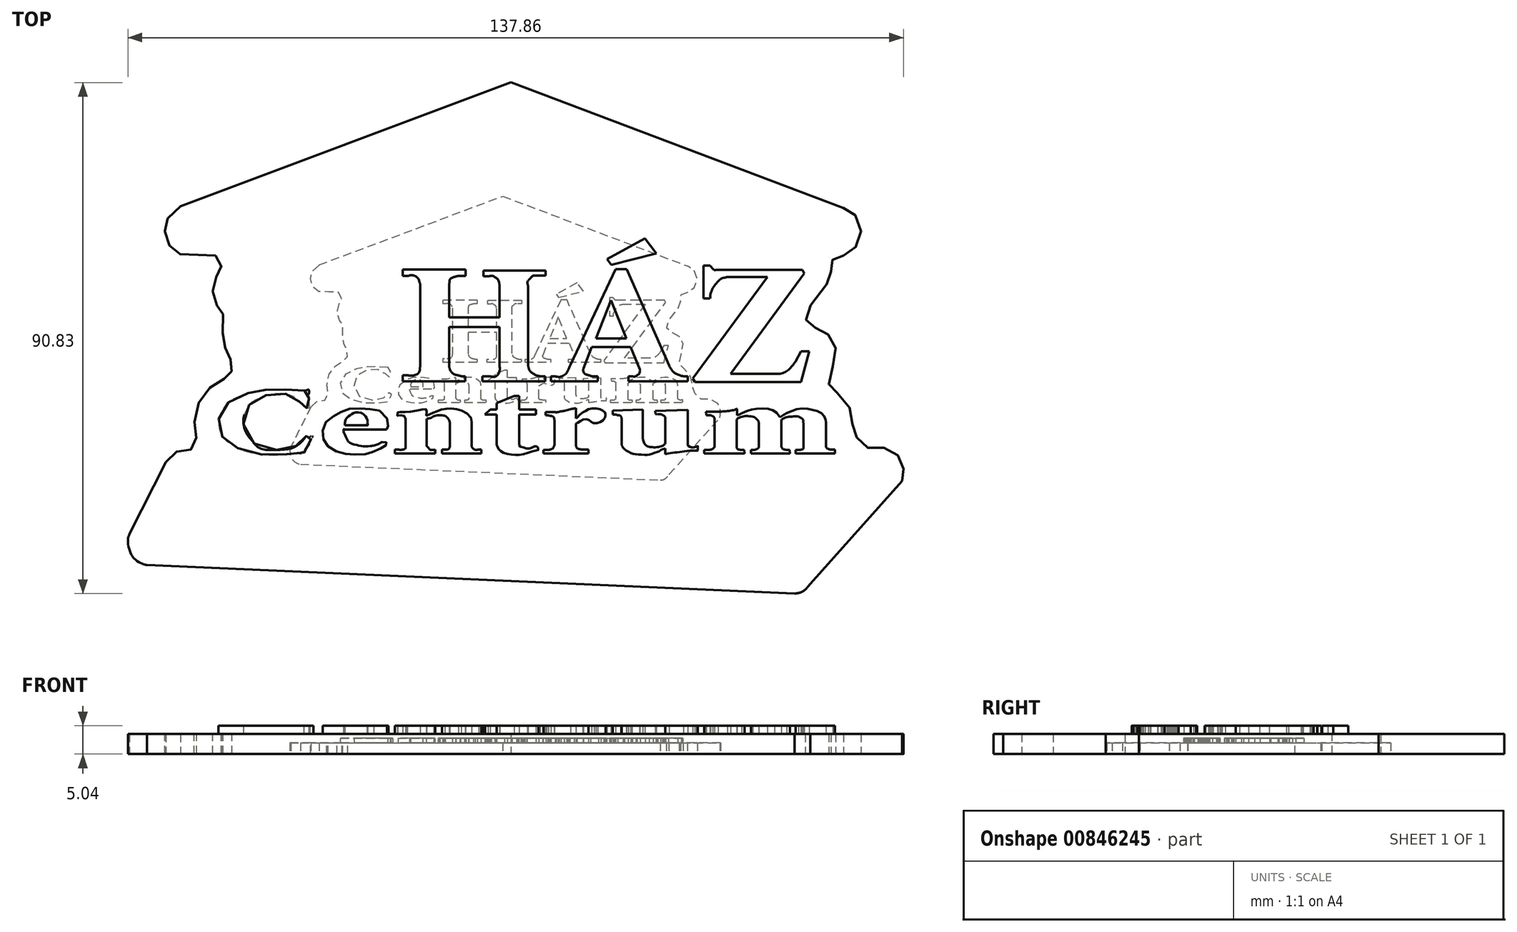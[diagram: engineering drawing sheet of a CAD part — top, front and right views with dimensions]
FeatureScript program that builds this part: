
annotation { "Feature Type Name" : "Feature", "Feature Type Description" : "" }
export const myFeature = defineFeature(function(context is Context, id is Id, definition is map)
    precondition{}
    {
        {
            var Q0;
            Q0=qCreatedBy(makeId("Top.planeOp"),FACE);
            var sketch = newSketch(context, id + "F0", { "sketchPlane" : qUnion([Q0])});
            skLineSegment(sketch, "E0", {"start": v(-30.08, 10.5) * mm, "end": v(1.83, 22.46) * mm});
            skLineSegment(sketch, "E1", {"start": v(1.83, 22.46) * mm, "end": v(33.46, 10.5) * mm});
            skLineSegment(sketch, "E2", {"start": v(33.46, 10.5) * mm, "end": v(-30.08, 10.5) * mm});
            skLineSegment(sketch, "E3", {"start": v(-30.08, -13.2) * mm, "end": v(37.96, -13.19) * mm});
            skLineSegment(sketch, "E4", {"start": v(37.96, -13.19) * mm, "end": v(29.5, -22.68) * mm});
            skLineSegment(sketch, "E5", {"start": v(29.5, -22.68) * mm, "end": v(-33.48, -19.9) * mm});
            skLineSegment(sketch, "E6", {"start": v(-33.48, -19.9) * mm, "end": v(-30.08, -13.2) * mm});
            skFitSpline(sketch, "E7", {"points": [v(-25.1, 4.44) * mm, v(-24.51, 4.46) * mm, v(-24.23, 4.28) * mm, v(-24.13, 3.89) * mm, v(-24.05, 0) * mm, v(-24.04, -0.4) * mm, v(-23.47, -1.49) * mm, v(-21.36, -2.34) * mm, v(-19.33, -2.17) * mm, v(-17.82, -0.87) * mm, v(-17.52, 0.4) * mm, v(-17.44, 3.46) * mm, v(-17.44, 3.92) * mm, v(-17.28, 4.2) * mm, v(-16.7, 4.4) * mm, v(-16.38, 4.41) * mm, v(-16.38, 4.8) * mm, v(-16.52, 4.86) * mm, v(-19.36, 4.89) * mm, v(-19.5, 4.87) * mm, v(-19.5, 4.8) * mm, v(-19.5, 4.47) * mm, v(-19.49, 4.38) * mm, v(-19.23, 4.43) * mm, v(-18.68, 4.41) * mm, v(-18.33, 4.24) * mm, v(-18.19, 3.78) * mm, v(-18.19, 3.5) * mm, v(-18.2, 0.13) * mm, v(-18.2, -0.14) * mm, v(-18.42, -0.62) * mm, v(-19.42, -1.46) * mm, v(-20.82, -1.61) * mm, v(-21.7, -1.14) * mm, v(-22.28, -0.2) * mm, v(-22.3, 0.46) * mm, v(-22.3, 0.68) * mm, v(-22.28, 3.9) * mm, v(-22.25, 4.08) * mm, v(-22.12, 4.32) * mm, v(-21.64, 4.43) * mm, v(-21.37, 4.43) * mm, v(-21.31, 4.6) * mm, v(-21.34, 4.74) * mm, v(-21.34, 4.89) * mm, v(-21.52, 4.89) * mm, v(-24.93, 4.84) * mm, v(-25.08, 4.86) * mm, v(-25.13, 4.71) * mm, v(-25.1, 4.44) * mm]});
            skLineSegment(sketch, "E8", {"start": v(-21.44, 5.5) * mm, "end": v(-21.2, 5.16) * mm});
            skLineSegment(sketch, "E9", {"start": v(-21.2, 5.16) * mm, "end": v(-18.55, 5.87) * mm});
            skLineSegment(sketch, "E10", {"start": v(-18.55, 5.87) * mm, "end": v(-19.2, 6.79) * mm});
            skLineSegment(sketch, "E11", {"start": v(-19.2, 6.79) * mm, "end": v(-21.44, 5.5) * mm});
            skLineSegment(sketch, "E12", {"start": v(-15.1, 4.36) * mm, "end": v(-15.63, 4.36) * mm});
            skLineSegment(sketch, "E13", {"start": v(-15.63, 4.36) * mm, "end": v(-15.63, 4.86) * mm});
            skLineSegment(sketch, "E14", {"start": v(-15.63, 4.86) * mm, "end": v(-11.81, 4.86) * mm});
            skLineSegment(sketch, "E15", {"start": v(-11.81, 4.86) * mm, "end": v(-11.81, 4.4) * mm});
            skLineSegment(sketch, "E16", {"start": v(-11.81, 4.4) * mm, "end": v(-12.34, 4.4) * mm});
            skLineSegment(sketch, "E17", {"start": v(-14.68, 4.01) * mm, "end": v(-14.68, -2.04) * mm});
            skLineSegment(sketch, "E18", {"start": v(-12.84, 4) * mm, "end": v(-12.84, -1.76) * mm});
            skFitSpline(sketch, "E19", {"points": [v(-15.1, 4.36) * mm, v(-14.78, 4.36) * mm, v(-14.68, 4.01) * mm], "startDerivative": vector(0.76, 0.17) * mm, "endDerivative": vector(0.08, -0.96) * mm});
            skFitSpline(sketch, "E20", {"points": [v(-12.84, 4) * mm, v(-12.68, 4.32) * mm, v(-12.34, 4.4) * mm], "startDerivative": vector(0.22, 0.75) * mm, "endDerivative": vector(0.8, 0.04) * mm});
            skFitSpline(sketch, "E21", {"points": [v(-14.68, -2.04) * mm, v(-14.68, -2.66) * mm, v(-14.68, -2.79) * mm, v(-15.17, -3.3) * mm, v(-15.78, -3.58) * mm, v(-15.9, -3.58) * mm, v(-15.89, -3.66) * mm, v(-15.9, -3.93) * mm, v(-15.78, -3.95) * mm, v(-15.43, -3.95) * mm, v(-14.92, -3.79) * mm, v(-13.75, -3.09) * mm, v(-13.2, -2.47) * mm, v(-12.84, -1.76) * mm], "startDerivative": vector(-0.26, -8.21) * mm, "endDerivative": vector(3.35, 7.13) * mm});
            skLineSegment(sketch, "E22", {"start": v(-8.39, 6.17) * mm, "end": v(-8.85, 6.17) * mm});
            skLineSegment(sketch, "E23", {"start": v(-8.85, 6.17) * mm, "end": v(-8.85, 6.78) * mm});
            skLineSegment(sketch, "E24", {"start": v(-8.85, 6.78) * mm, "end": v(-2.66, 6.78) * mm});
            skLineSegment(sketch, "E25", {"start": v(-2.66, 6.78) * mm, "end": v(-2.66, 6.17) * mm});
            skLineSegment(sketch, "E26", {"start": v(-2.66, 6.17) * mm, "end": v(-3.36, 6.17) * mm});
            skLineSegment(sketch, "E27", {"start": v(-7.13, 5.37) * mm, "end": v(-7.13, -2.82) * mm});
            skLineSegment(sketch, "E28", {"start": v(-4.27, 5.39) * mm, "end": v(-4.27, 2.06) * mm});
            skLineSegment(sketch, "E29", {"start": v(-4.27, 2.06) * mm, "end": v(0.72, 2.06) * mm});
            skLineSegment(sketch, "E30", {"start": v(0.72, 2.06) * mm, "end": v(0.72, 5.28) * mm});
            skLineSegment(sketch, "E31", {"start": v(-0.41, 6.13) * mm, "end": v(-0.88, 6.13) * mm});
            skLineSegment(sketch, "E32", {"start": v(-0.88, 6.13) * mm, "end": v(-0.88, 6.7) * mm});
            skLineSegment(sketch, "E33", {"start": v(-0.88, 6.7) * mm, "end": v(5.27, 6.7) * mm});
            skLineSegment(sketch, "E34", {"start": v(5.27, 6.7) * mm, "end": v(5.27, 6.19) * mm});
            skLineSegment(sketch, "E35", {"start": v(5.27, 6.19) * mm, "end": v(4.53, 6.19) * mm});
            skLineSegment(sketch, "E36", {"start": v(3.5, 5.2) * mm, "end": v(3.5, -2.7) * mm});
            skLineSegment(sketch, "E37", {"start": v(-4.28, -2.78) * mm, "end": v(-4.28, 1.1) * mm});
            skLineSegment(sketch, "E38", {"start": v(-4.28, 1.1) * mm, "end": v(0.7, 1.1) * mm});
            skLineSegment(sketch, "E39", {"start": v(0.7, 1.1) * mm, "end": v(0.7, -2.6) * mm});
            skLineSegment(sketch, "E40", {"start": v(-8.5, -3.66) * mm, "end": v(-8.85, -3.66) * mm});
            skLineSegment(sketch, "E41", {"start": v(-8.85, -3.66) * mm, "end": v(-8.85, -4.23) * mm});
            skLineSegment(sketch, "E42", {"start": v(-8.85, -4.23) * mm, "end": v(-2.68, -4.23) * mm});
            skLineSegment(sketch, "E43", {"start": v(-2.68, -4.23) * mm, "end": v(-2.68, -3.75) * mm});
            skLineSegment(sketch, "E44", {"start": v(-2.68, -3.75) * mm, "end": v(-3.08, -3.75) * mm});
            skLineSegment(sketch, "E45", {"start": v(-0.67, -3.75) * mm, "end": v(-1, -3.75) * mm});
            skLineSegment(sketch, "E46", {"start": v(-1, -3.75) * mm, "end": v(-1, -4.23) * mm});
            skLineSegment(sketch, "E47", {"start": v(-1, -4.23) * mm, "end": v(5.21, -4.23) * mm});
            skLineSegment(sketch, "E48", {"start": v(5.21, -4.23) * mm, "end": v(5.21, -3.75) * mm});
            skLineSegment(sketch, "E49", {"start": v(5.21, -3.75) * mm, "end": v(4.72, -3.75) * mm});
            skLineSegment(sketch, "E50", {"start": v(6.1, -3.75) * mm, "end": v(5.78, -3.75) * mm});
            skLineSegment(sketch, "E51", {"start": v(5.78, -3.75) * mm, "end": v(5.78, -4.23) * mm});
            skLineSegment(sketch, "E52", {"start": v(5.78, -4.23) * mm, "end": v(10.42, -4.23) * mm});
            skLineSegment(sketch, "E53", {"start": v(10.42, -4.23) * mm, "end": v(10.42, -3.75) * mm});
            skLineSegment(sketch, "E54", {"start": v(10.42, -3.75) * mm, "end": v(10.07, -3.75) * mm});
            skLineSegment(sketch, "E55", {"start": v(7.73, -2.6) * mm, "end": v(12.18, 6.83) * mm});
            skLineSegment(sketch, "E56", {"start": v(12.18, 6.83) * mm, "end": v(13.26, 6.83) * mm});
            skLineSegment(sketch, "E57", {"start": v(13.26, 6.83) * mm, "end": v(17.45, -2.7) * mm});
            skLineSegment(sketch, "E58", {"start": v(10.22, 0) * mm, "end": v(11.72, 3.76) * mm});
            skLineSegment(sketch, "E59", {"start": v(11.72, 3.76) * mm, "end": v(13.22, 0) * mm});
            skLineSegment(sketch, "E60", {"start": v(13.22, 0) * mm, "end": v(10.22, 0) * mm});
            skLineSegment(sketch, "E61", {"start": v(8.99, -3) * mm, "end": v(9.81, -0.88) * mm});
            skLineSegment(sketch, "E62", {"start": v(9.81, -0.88) * mm, "end": v(13.66, -0.88) * mm});
            skLineSegment(sketch, "E63", {"start": v(13.66, -0.88) * mm, "end": v(14.56, -3.07) * mm});
            skLineSegment(sketch, "E64", {"start": v(13.8, -3.75) * mm, "end": v(13.43, -3.75) * mm});
            skLineSegment(sketch, "E65", {"start": v(13.43, -3.75) * mm, "end": v(13.43, -4.23) * mm});
            skLineSegment(sketch, "E66", {"start": v(13.43, -4.23) * mm, "end": v(19.3, -4.23) * mm});
            skLineSegment(sketch, "E67", {"start": v(19.3, -4.23) * mm, "end": v(19.3, -3.75) * mm});
            skLineSegment(sketch, "E68", {"start": v(19.3, -3.75) * mm, "end": v(18.88, -3.75) * mm});
            skLineSegment(sketch, "E69", {"start": v(11.34, 7.83) * mm, "end": v(11.73, 7.26) * mm});
            skLineSegment(sketch, "E70", {"start": v(11.73, 7.26) * mm, "end": v(16.2, 8.38) * mm});
            skLineSegment(sketch, "E71", {"start": v(16.2, 8.38) * mm, "end": v(15.06, 9.86) * mm});
            skLineSegment(sketch, "E72", {"start": v(15.06, 9.86) * mm, "end": v(11.34, 7.83) * mm});
            skLineSegment(sketch, "E73", {"start": v(23.23, 6.07) * mm, "end": v(27.17, 6.07) * mm});
            skLineSegment(sketch, "E74", {"start": v(27.17, 6.07) * mm, "end": v(19.8, -3.96) * mm});
            skLineSegment(sketch, "E75", {"start": v(19.8, -3.96) * mm, "end": v(20, -4.32) * mm});
            skLineSegment(sketch, "E76", {"start": v(20, -4.32) * mm, "end": v(30.47, -4.32) * mm});
            skLineSegment(sketch, "E77", {"start": v(30.47, -4.32) * mm, "end": v(31.28, -1.27) * mm});
            skLineSegment(sketch, "E78", {"start": v(31.28, -1.27) * mm, "end": v(30.49, -1.27) * mm});
            skLineSegment(sketch, "E79", {"start": v(30.49, -1.27) * mm, "end": v(29.93, -2.28) * mm});
            skLineSegment(sketch, "E80", {"start": v(27.89, -3.5) * mm, "end": v(23.51, -3.5) * mm});
            skLineSegment(sketch, "E81", {"start": v(23.51, -3.5) * mm, "end": v(30.8, 6.4) * mm});
            skLineSegment(sketch, "E82", {"start": v(30.8, 6.4) * mm, "end": v(30.6, 6.77) * mm});
            skLineSegment(sketch, "E83", {"start": v(30.6, 6.77) * mm, "end": v(22.29, 6.77) * mm});
            skLineSegment(sketch, "E84", {"start": v(21.5, 7.2) * mm, "end": v(20.84, 7.2) * mm});
            skLineSegment(sketch, "E85", {"start": v(20.84, 7.2) * mm, "end": v(20.84, 3.95) * mm});
            skLineSegment(sketch, "E86", {"start": v(20.84, 3.95) * mm, "end": v(21.5, 3.95) * mm});
            skFitSpline(sketch, "E87", {"points": [v(-8.39, 6.17) * mm, v(-7.89, 6.17) * mm, v(-7.38, 5.86) * mm, v(-7.13, 5.37) * mm], "startDerivative": vector(1.55, 0.19) * mm, "endDerivative": vector(0.57, -1.56) * mm});
            skFitSpline(sketch, "E88", {"points": [v(-4.27, 5.39) * mm, v(-4.1, 5.83) * mm, v(-3.74, 6.05) * mm, v(-3.36, 6.17) * mm], "startDerivative": vector(0.33, 1.4) * mm, "endDerivative": vector(1.17, 0.33) * mm});
            skFitSpline(sketch, "E89", {"points": [v(-7.13, -2.82) * mm, v(-7.28, -3.3) * mm, v(-7.7, -3.6) * mm, v(-8.23, -3.66) * mm, v(-8.5, -3.66) * mm], "startDerivative": vector(-0.35, -1.9) * mm, "endDerivative": vector(-1.25, 0.02) * mm});
            skFitSpline(sketch, "E90", {"points": [v(-4.28, -2.78) * mm, v(-4.1, -3.18) * mm, v(-3.76, -3.5) * mm, v(-3.08, -3.75) * mm], "startDerivative": vector(0.48, -1.4) * mm, "endDerivative": vector(1.91, -0.58) * mm});
            skFitSpline(sketch, "E91", {"points": [v(-0.67, -3.75) * mm, v(-0.24, -3.75) * mm, v(0.3, -3.66) * mm, v(0.65, -3.2) * mm, v(0.7, -2.6) * mm], "startDerivative": vector(1.82, 0) * mm, "endDerivative": vector(-0.04, 2.27) * mm});
            skFitSpline(sketch, "E92", {"points": [v(3.5, -2.7) * mm, v(3.72, -3.17) * mm, v(4.05, -3.48) * mm, v(4.41, -3.66) * mm, v(4.72, -3.75) * mm], "startDerivative": vector(0.63, -1.81) * mm, "endDerivative": vector(1.39, -0.34) * mm});
            skFitSpline(sketch, "E93", {"points": [v(6.1, -3.75) * mm, v(6.63, -3.75) * mm, v(7.2, -3.43) * mm, v(7.73, -2.6) * mm], "startDerivative": vector(1.82, -0.19) * mm, "endDerivative": vector(1.2, 2.39) * mm});
            skFitSpline(sketch, "E94", {"points": [v(8.99, -3) * mm, v(8.99, -3.18) * mm, v(9.13, -3.44) * mm, v(9.5, -3.63) * mm, v(10.07, -3.75) * mm], "startDerivative": vector(-0.22, -1.52) * mm, "endDerivative": vector(2.37, -0.06) * mm});
            skFitSpline(sketch, "E95", {"points": [v(-0.41, 6.13) * mm, v(0, 6.13) * mm, v(0.32, 5.98) * mm, v(0.54, 5.77) * mm, v(0.67, 5.45) * mm, v(0.72, 5.28) * mm], "startDerivative": vector(1.85, 0.19) * mm, "endDerivative": vector(0.28, -1) * mm});
            skFitSpline(sketch, "E96", {"points": [v(3.5, 5.2) * mm, v(3.5, 5.55) * mm, v(3.71, 5.87) * mm, v(4.07, 6.13) * mm, v(4.53, 6.19) * mm], "startDerivative": vector(-0.19, 1.53) * mm, "endDerivative": vector(1.8, 0.02) * mm});
            skFitSpline(sketch, "E97", {"points": [v(13.8, -3.75) * mm, v(14.03, -3.75) * mm, v(14.36, -3.59) * mm, v(14.5, -3.41) * mm, v(14.56, -3.07) * mm], "startDerivative": vector(0.97, -0.13) * mm, "endDerivative": vector(0.08, 1.38) * mm});
            skFitSpline(sketch, "E98", {"points": [v(17.45, -2.7) * mm, v(17.64, -2.98) * mm, v(17.94, -3.34) * mm, v(18.22, -3.52) * mm, v(18.6, -3.68) * mm, v(18.88, -3.75) * mm], "startDerivative": vector(0.89, -1.38) * mm, "endDerivative": vector(1.49, -0.33) * mm});
            skFitSpline(sketch, "E99", {"points": [v(21.5, 7.2) * mm, v(21.67, 6.98) * mm, v(21.93, 6.8) * mm, v(22.29, 6.77) * mm], "startDerivative": vector(0.55, -0.66) * mm, "endDerivative": vector(1.06, 0.06) * mm});
            skFitSpline(sketch, "E100", {"points": [v(21.5, 3.95) * mm, v(21.57, 4.4) * mm, v(21.78, 4.93) * mm, v(22.1, 5.4) * mm, v(22.64, 5.85) * mm, v(23.23, 6.07) * mm], "startDerivative": vector(0.3, 2.51) * mm, "endDerivative": vector(2.87, 0.8) * mm});
            skFitSpline(sketch, "E101", {"points": [v(27.89, -3.5) * mm, v(28.28, -3.5) * mm, v(28.84, -3.34) * mm, v(29.28, -3.05) * mm, v(29.7, -2.6) * mm, v(29.93, -2.28) * mm], "startDerivative": vector(2.09, -0.14) * mm, "endDerivative": vector(1.15, 1.72) * mm});
            skFitSpline(sketch, "E102", {"points": [v(-18.55, -5.16) * mm, v(-19.5, -5.13) * mm, v(-21.12, -5.07) * mm, v(-22, -5.07) * mm, v(-22.58, -5.12) * mm, v(-23.16, -5.22) * mm, v(-23.92, -5.38) * mm, v(-24.9, -5.72) * mm, v(-25.9, -6.27) * mm, v(-26.51, -6.9) * mm, v(-26.87, -7.57) * mm, v(-27, -8.39) * mm, v(-26.85, -9.23) * mm, v(-26.55, -9.8) * mm, v(-26.01, -10.28) * mm, v(-25.25, -10.75) * mm, v(-23.93, -11.23) * mm, v(-22.44, -11.46) * mm, v(-20.86, -11.5) * mm, v(-19.93, -11.43) * mm, v(-19.02, -11.34) * mm, v(-18.6, -11.26) * mm, v(-18.57, -11.26) * mm, v(-18.48, -11.07) * mm, v(-18.1, -10.43) * mm, v(-17.75, -9.8) * mm, v(-17.71, -9.74) * mm, v(-17.8, -9.71) * mm, v(-18.35, -9.68) * mm, v(-18.4, -9.67) * mm, v(-18.46, -9.74) * mm, v(-18.56, -9.88) * mm, v(-18.93, -10.27) * mm, v(-19.68, -10.75) * mm, v(-20.35, -10.95) * mm, v(-21.57, -11) * mm, v(-22.99, -10.7) * mm, v(-23.78, -10.03) * mm, v(-24.3, -9.17) * mm, v(-24.47, -7.92) * mm, v(-24.2, -6.98) * mm, v(-23.84, -6.46) * mm, v(-23.06, -5.94) * mm, v(-22.3, -5.64) * mm, v(-21.27, -5.47) * mm, v(-20.47, -5.49) * mm, v(-20, -5.61) * mm, v(-19.36, -5.96) * mm, v(-18.97, -6.34) * mm, v(-18.7, -6.63) * mm, v(-18.63, -6.81) * mm, v(-18.62, -6.84) * mm, v(-18.53, -6.87) * mm, v(-18.08, -6.84) * mm, v(-18.05, -6.82) * mm, v(-18.08, -6.52) * mm, v(-18.1, -6.12) * mm, v(-18.13, -5.6) * mm, v(-18.22, -5.17) * mm, v(-18.55, -5.16) * mm]});
            skLineSegment(sketch, "E103", {"start": v(-14.56, -8.57) * mm, "end": v(-12.39, -8.57) * mm});
            skLineSegment(sketch, "E104", {"start": v(-14.61, -9) * mm, "end": v(-10.44, -9) * mm});
            skLineSegment(sketch, "E105", {"start": v(-9.34, -11) * mm, "end": v(-9.63, -11) * mm});
            skLineSegment(sketch, "E106", {"start": v(-9.63, -11) * mm, "end": v(-9.63, -11.37) * mm});
            skLineSegment(sketch, "E107", {"start": v(-9.63, -11.37) * mm, "end": v(-5.63, -11.37) * mm});
            skLineSegment(sketch, "E108", {"start": v(-5.63, -11.37) * mm, "end": v(-5.63, -10.98) * mm});
            skLineSegment(sketch, "E109", {"start": v(-5.63, -10.98) * mm, "end": v(-5.8, -11) * mm});
            skLineSegment(sketch, "E110", {"start": v(-8.57, -7.94) * mm, "end": v(-8.57, -10.62) * mm});
            skLineSegment(sketch, "E111", {"start": v(-6.5, -7.96) * mm, "end": v(-6.5, -10.59) * mm});
            skLineSegment(sketch, "E112", {"start": v(-4.21, -8.3) * mm, "end": v(-4.21, -10.74) * mm});
            skLineSegment(sketch, "E113", {"start": v(-4.69, -10.98) * mm, "end": v(-4.98, -10.98) * mm});
            skLineSegment(sketch, "E114", {"start": v(-4.98, -10.98) * mm, "end": v(-4.98, -11.37) * mm});
            skLineSegment(sketch, "E115", {"start": v(-4.98, -11.37) * mm, "end": v(-1.1, -11.37) * mm});
            skLineSegment(sketch, "E116", {"start": v(-1.1, -11.37) * mm, "end": v(-1.1, -10.98) * mm});
            skLineSegment(sketch, "E117", {"start": v(-1.1, -10.98) * mm, "end": v(-1.33, -10.98) * mm});
            skLineSegment(sketch, "E118", {"start": v(-2.04, -8.28) * mm, "end": v(-2.04, -10.69) * mm});
            skLineSegment(sketch, "E119", {"start": v(2.64, -10.35) * mm, "end": v(2.64, -7.53) * mm});
            skLineSegment(sketch, "E120", {"start": v(2.64, -7.53) * mm, "end": v(4.31, -7.53) * mm});
            skLineSegment(sketch, "E121", {"start": v(4.31, -7.53) * mm, "end": v(4.31, -7.02) * mm});
            skLineSegment(sketch, "E122", {"start": v(4.31, -7.02) * mm, "end": v(2.64, -7.02) * mm});
            skLineSegment(sketch, "E123", {"start": v(2.64, -7.02) * mm, "end": v(2.64, -5.7) * mm});
            skLineSegment(sketch, "E124", {"start": v(2.64, -5.7) * mm, "end": v(2.15, -5.7) * mm});
            skLineSegment(sketch, "E125", {"start": v(2.15, -5.7) * mm, "end": v(0.43, -6.4) * mm});
            skLineSegment(sketch, "E126", {"start": v(0.43, -6.4) * mm, "end": v(0.43, -7.02) * mm});
            skLineSegment(sketch, "E127", {"start": v(0.43, -7.02) * mm, "end": v(-0.2, -7.02) * mm});
            skLineSegment(sketch, "E128", {"start": v(-0.2, -7.02) * mm, "end": v(-0.73, -7.53) * mm});
            skLineSegment(sketch, "E129", {"start": v(-0.73, -7.53) * mm, "end": v(0.43, -7.53) * mm});
            skLineSegment(sketch, "E130", {"start": v(0.43, -7.53) * mm, "end": v(0.43, -10.53) * mm});
            skLineSegment(sketch, "E131", {"start": v(6.13, -8.07) * mm, "end": v(6.13, -10.53) * mm});
            skLineSegment(sketch, "E132", {"start": v(8.26, -8.42) * mm, "end": v(8.26, -10.6) * mm});
            skLineSegment(sketch, "E133", {"start": v(5.37, -11) * mm, "end": v(5.06, -11) * mm});
            skLineSegment(sketch, "E134", {"start": v(5.06, -11) * mm, "end": v(5.06, -11.36) * mm});
            skLineSegment(sketch, "E135", {"start": v(5.06, -11.36) * mm, "end": v(9.5, -11.36) * mm});
            skLineSegment(sketch, "E136", {"start": v(9.5, -11.36) * mm, "end": v(9.5, -10.98) * mm});
            skLineSegment(sketch, "E137", {"start": v(9.5, -10.98) * mm, "end": v(8.93, -10.98) * mm});
            skLineSegment(sketch, "E138", {"start": v(8.26, -7.93) * mm, "end": v(8.26, -6.9) * mm});
            skLineSegment(sketch, "E139", {"start": v(5.53, -7.62) * mm, "end": v(5.24, -7.62) * mm});
            skLineSegment(sketch, "E140", {"start": v(5.24, -7.62) * mm, "end": v(5.24, -7.3) * mm});
            skLineSegment(sketch, "E141", {"start": v(5.24, -7.3) * mm, "end": v(6.13, -7.3) * mm});
            skLineSegment(sketch, "E142", {"start": v(14.85, -9.91) * mm, "end": v(14.85, -7.04) * mm});
            skLineSegment(sketch, "E143", {"start": v(14.85, -7.04) * mm, "end": v(11.89, -7.14) * mm});
            skLineSegment(sketch, "E144", {"start": v(11.89, -7.14) * mm, "end": v(11.9, -7.54) * mm});
            skLineSegment(sketch, "E145", {"start": v(12.77, -7.86) * mm, "end": v(12.77, -10.35) * mm});
            skLineSegment(sketch, "E146", {"start": v(19.3, -10.56) * mm, "end": v(19.3, -7.08) * mm});
            skLineSegment(sketch, "E147", {"start": v(19.3, -7.08) * mm, "end": v(16.1, -7.17) * mm});
            skLineSegment(sketch, "E148", {"start": v(16.1, -7.17) * mm, "end": v(16.11, -7.5) * mm});
            skLineSegment(sketch, "E149", {"start": v(17.07, -7.77) * mm, "end": v(17.07, -10.43) * mm});
            skLineSegment(sketch, "E150", {"start": v(17.06, -10.88) * mm, "end": v(17.06, -11.45) * mm});
            skLineSegment(sketch, "E151", {"start": v(21.75, -7.23) * mm, "end": v(21.11, -7.23) * mm});
            skLineSegment(sketch, "E152", {"start": v(21.11, -7.23) * mm, "end": v(21.12, -7.6) * mm});
            skLineSegment(sketch, "E153", {"start": v(21.12, -7.6) * mm, "end": v(21.56, -7.6) * mm});
            skLineSegment(sketch, "E154", {"start": v(21.94, -7.89) * mm, "end": v(21.94, -10.72) * mm});
            skLineSegment(sketch, "E155", {"start": v(24.11, -8.08) * mm, "end": v(24.11, -10.75) * mm});
            skLineSegment(sketch, "E156", {"start": v(26.3, -8.31) * mm, "end": v(26.3, -10.76) * mm});
            skLineSegment(sketch, "E157", {"start": v(28.55, -8.04) * mm, "end": v(28.55, -10.73) * mm});
            skLineSegment(sketch, "E158", {"start": v(30.73, -8.35) * mm, "end": v(30.73, -10.82) * mm});
            skLineSegment(sketch, "E159", {"start": v(32.95, -8.3) * mm, "end": v(32.95, -10.75) * mm});
            skLineSegment(sketch, "E160", {"start": v(21.07, -11.02) * mm, "end": v(20.93, -11.02) * mm});
            skLineSegment(sketch, "E161", {"start": v(20.93, -11.02) * mm, "end": v(20.93, -11.4) * mm});
            skLineSegment(sketch, "E162", {"start": v(20.93, -11.4) * mm, "end": v(24.9, -11.4) * mm});
            skLineSegment(sketch, "E163", {"start": v(24.9, -11.4) * mm, "end": v(24.88, -11) * mm});
            skLineSegment(sketch, "E164", {"start": v(24.88, -11) * mm, "end": v(24.61, -11.02) * mm});
            skLineSegment(sketch, "E165", {"start": v(25.73, -11) * mm, "end": v(25.55, -11) * mm});
            skLineSegment(sketch, "E166", {"start": v(25.55, -11) * mm, "end": v(25.55, -11.4) * mm});
            skLineSegment(sketch, "E167", {"start": v(25.55, -11.4) * mm, "end": v(29.38, -11.4) * mm});
            skLineSegment(sketch, "E168", {"start": v(29.38, -11.4) * mm, "end": v(29.36, -11) * mm});
            skLineSegment(sketch, "E169", {"start": v(29.36, -11) * mm, "end": v(29.06, -11.02) * mm});
            skLineSegment(sketch, "E170", {"start": v(30.22, -11) * mm, "end": v(29.94, -11) * mm});
            skLineSegment(sketch, "E171", {"start": v(29.94, -11) * mm, "end": v(29.94, -11.4) * mm});
            skLineSegment(sketch, "E172", {"start": v(29.94, -11.4) * mm, "end": v(33.83, -11.4) * mm});
            skLineSegment(sketch, "E173", {"start": v(33.83, -11.4) * mm, "end": v(33.83, -10.97) * mm});
            skLineSegment(sketch, "E174", {"start": v(33.83, -10.97) * mm, "end": v(33.61, -10.98) * mm});
            skLineSegment(sketch, "E175", {"start": v(24.15, -7.62) * mm, "end": v(24.15, -6.96) * mm});
            skFitSpline(sketch, "E176", {"points": [v(33.61, -10.98) * mm, v(33.42, -10.98) * mm, v(33.1, -10.86) * mm, v(32.95, -10.75) * mm], "startDerivative": vector(-0.59, -0.06) * mm, "endDerivative": vector(-0.4, 0.42) * mm});
            skFitSpline(sketch, "E177", {"points": [v(32.95, -8.3) * mm, v(32.85, -7.9) * mm, v(32.66, -7.6) * mm, v(32.23, -7.27) * mm, v(31.7, -7.1) * mm, v(31.1, -6.98) * mm, v(30.3, -7) * mm, v(29.68, -7.15) * mm, v(29.1, -7.4) * mm, v(28.67, -7.62) * mm, v(28.4, -7.78) * mm, v(28.36, -7.79) * mm, v(28.32, -7.7) * mm, v(27.99, -7.33) * mm, v(27.45, -7.06) * mm, v(26.78, -6.96) * mm, v(25.91, -7) * mm, v(25.4, -7.11) * mm, v(24.68, -7.38) * mm, v(24.41, -7.52) * mm, v(24.15, -7.62) * mm], "startDerivative": vector(-1.81, 8.83) * mm, "endDerivative": vector(-7.1, -2.45) * mm});
            skFitSpline(sketch, "E178", {"points": [v(30.22, -11) * mm, v(30.4, -11) * mm, v(30.6, -10.96) * mm, v(30.73, -10.82) * mm], "startDerivative": vector(0.55, -0.04) * mm, "endDerivative": vector(0.32, 0.72) * mm});
            skFitSpline(sketch, "E179", {"points": [v(28.55, -10.73) * mm, v(28.68, -10.9) * mm, v(28.84, -10.97) * mm, v(29.06, -11.02) * mm], "startDerivative": vector(0.37, -0.56) * mm, "endDerivative": vector(0.68, -0.1) * mm});
            skFitSpline(sketch, "E180", {"points": [v(28.55, -8.04) * mm, v(28.7, -7.94) * mm, v(29.24, -7.76) * mm, v(29.59, -7.73) * mm, v(29.95, -7.73) * mm, v(30.43, -7.87) * mm, v(30.68, -8.15) * mm, v(30.73, -8.35) * mm], "startDerivative": vector(1.2, 0.86) * mm, "endDerivative": vector(1.1, -1.57) * mm});
            skFitSpline(sketch, "E181", {"points": [v(26.3, -8.31) * mm, v(26.23, -8.14) * mm, v(26.06, -7.96) * mm, v(25.87, -7.82) * mm, v(25.27, -7.7) * mm, v(24.9, -7.7) * mm, v(24.36, -7.86) * mm, v(24.19, -7.96) * mm, v(24.11, -8.08) * mm], "startDerivative": vector(-0.53, 1.8) * mm, "endDerivative": vector(-0.74, -1.45) * mm});
            skFitSpline(sketch, "E182", {"points": [v(25.73, -11) * mm, v(25.87, -11) * mm, v(26.05, -10.96) * mm, v(26.23, -10.86) * mm, v(26.3, -10.76) * mm], "startDerivative": vector(0.62, -0.04) * mm, "endDerivative": vector(0.28, 0.48) * mm});
            skFitSpline(sketch, "E183", {"points": [v(24.11, -10.75) * mm, v(24.17, -10.86) * mm, v(24.29, -10.96) * mm, v(24.5, -11) * mm, v(24.61, -11.02) * mm], "startDerivative": vector(0.2, -0.51) * mm, "endDerivative": vector(0.46, -0.05) * mm});
            skFitSpline(sketch, "E184", {"points": [v(24.15, -6.96) * mm, v(23.92, -7.04) * mm, v(22.83, -7.2) * mm, v(21.75, -7.23) * mm], "startDerivative": vector(-0.95, -0.4) * mm, "endDerivative": vector(-2.53, -0.03) * mm});
            skFitSpline(sketch, "E185", {"points": [v(21.56, -7.6) * mm, v(21.67, -7.65) * mm, v(21.86, -7.77) * mm, v(21.94, -7.89) * mm], "startDerivative": vector(0.36, -0.15) * mm, "endDerivative": vector(0.2, -0.4) * mm});
            skFitSpline(sketch, "E186", {"points": [v(21.94, -10.72) * mm, v(21.87, -10.8) * mm, v(21.68, -10.93) * mm, v(21.26, -11.02) * mm, v(21.07, -11.02) * mm], "startDerivative": vector(-0.28, -0.62) * mm, "endDerivative": vector(-0.73, 0.03) * mm});
            skFitSpline(sketch, "E187", {"points": [v(17.06, -11.45) * mm, v(17.7, -11.33) * mm, v(18.22, -11.26) * mm, v(18.78, -11.19) * mm, v(19.6, -11.1) * mm, v(20.24, -11.1) * mm, v(20.27, -11.09) * mm, v(20.27, -10.9) * mm, v(20.24, -10.72) * mm, v(19.91, -10.72) * mm, v(19.3, -10.56) * mm], "startDerivative": vector(3.34, 1) * mm, "endDerivative": vector(-2.67, 2.3) * mm});
            skFitSpline(sketch, "E188", {"points": [v(16.11, -7.5) * mm, v(16.3, -7.5) * mm, v(16.55, -7.5) * mm, v(16.84, -7.6) * mm, v(17.07, -7.77) * mm], "startDerivative": vector(0.84, -0.02) * mm, "endDerivative": vector(0.84, -0.69) * mm});
            skFitSpline(sketch, "E189", {"points": [v(14.85, -9.91) * mm, v(14.93, -10.17) * mm, v(15.05, -10.4) * mm, v(15.4, -10.67) * mm, v(15.7, -10.74) * mm, v(16.11, -10.75) * mm, v(16.52, -10.7) * mm, v(16.8, -10.6) * mm, v(17.07, -10.43) * mm], "startDerivative": vector(0.65, -2.37) * mm, "endDerivative": vector(2.2, 1.56) * mm});
            skFitSpline(sketch, "E190", {"points": [v(12.77, -10.35) * mm, v(12.77, -10.5) * mm, v(12.83, -10.66) * mm, v(12.98, -10.88) * mm, v(13.37, -11.15) * mm, v(13.88, -11.38) * mm, v(14.52, -11.47) * mm, v(15.32, -11.48) * mm, v(15.85, -11.36) * mm, v(16.43, -11.15) * mm, v(16.76, -11) * mm, v(17.06, -10.88) * mm], "startDerivative": vector(-0.25, -2.77) * mm, "endDerivative": vector(3.84, 1.33) * mm});
            skFitSpline(sketch, "E191", {"points": [v(11.9, -7.54) * mm, v(12.1, -7.54) * mm, v(12.4, -7.6) * mm, v(12.64, -7.7) * mm, v(12.77, -7.86) * mm], "startDerivative": vector(0.84, 0.04) * mm, "endDerivative": vector(0.44, -0.83) * mm});
            skFitSpline(sketch, "E192", {"points": [v(6.13, -7.3) * mm, v(6.3, -7.3) * mm, v(6.7, -7.23) * mm, v(7.26, -7.12) * mm, v(7.83, -6.98) * mm, v(8.26, -6.9) * mm], "startDerivative": vector(1.3, -0.06) * mm, "endDerivative": vector(2.6, 0.65) * mm});
            skFitSpline(sketch, "E193", {"points": [v(5.53, -7.62) * mm, v(5.66, -7.65) * mm, v(5.94, -7.73) * mm, v(6.07, -7.87) * mm, v(6.13, -8.07) * mm], "startDerivative": vector(0.58, -0.13) * mm, "endDerivative": vector(0.16, -0.83) * mm});
            skFitSpline(sketch, "E194", {"points": [v(6.13, -10.53) * mm, v(6.08, -10.68) * mm, v(5.97, -10.83) * mm, v(5.74, -10.96) * mm, v(5.49, -11.01) * mm, v(5.37, -11) * mm], "startDerivative": vector(-0.24, -0.84) * mm, "endDerivative": vector(-0.67, 0.05) * mm});
            skFitSpline(sketch, "E195", {"points": [v(8.26, -10.6) * mm, v(8.33, -10.78) * mm, v(8.47, -10.9) * mm, v(8.71, -10.96) * mm, v(8.93, -10.98) * mm], "startDerivative": vector(0.19, -0.8) * mm, "endDerivative": vector(0.81, -0.06) * mm});
            skFitSpline(sketch, "E196", {"points": [v(8.26, -7.93) * mm, v(8.42, -7.77) * mm, v(8.76, -7.45) * mm, v(9.12, -7.21) * mm, v(9.4, -7.05) * mm, v(9.84, -6.95) * mm, v(10.4, -6.96) * mm, v(10.76, -7.07) * mm, v(11.02, -7.25) * mm, v(11.15, -7.45) * mm, v(11.14, -7.64) * mm, v(11.04, -7.93) * mm, v(10.8, -8.17) * mm, v(10.54, -8.29) * mm, v(10.04, -8.35) * mm, v(9.8, -8.27) * mm, v(9.58, -8.12) * mm, v(9.37, -8.03) * mm, v(9.06, -8) * mm, v(8.86, -8.07) * mm, v(8.52, -8.27) * mm, v(8.26, -8.42) * mm], "startDerivative": vector(3.6, 3.57) * mm, "endDerivative": vector(-5.27, -3.1) * mm});
            skFitSpline(sketch, "E197", {"points": [v(0.43, -10.53) * mm, v(0.55, -10.8) * mm, v(0.84, -11.12) * mm, v(1.32, -11.34) * mm, v(2.07, -11.47) * mm, v(2.8, -11.46) * mm, v(3.75, -11.24) * mm, v(4.34, -11.07) * mm, v(4.5, -10.98) * mm, v(4.47, -10.79) * mm, v(4.35, -10.7) * mm, v(4.15, -10.69) * mm, v(3.9, -10.78) * mm, v(3.48, -10.86) * mm, v(3.02, -10.75) * mm, v(2.72, -10.6) * mm, v(2.64, -10.35) * mm], "startDerivative": vector(1.69, -5.06) * mm, "endDerivative": vector(-0.79, 5.58) * mm});
            skFitSpline(sketch, "E198", {"points": [v(-2.04, -10.69) * mm, v(-1.94, -10.84) * mm, v(-1.68, -10.98) * mm, v(-1.33, -10.98) * mm], "startDerivative": vector(0.27, -0.56) * mm, "endDerivative": vector(0.93, 0.1) * mm});
            skFitSpline(sketch, "E199", {"points": [v(-4.21, -10.74) * mm, v(-4.28, -10.87) * mm, v(-4.45, -10.97) * mm, v(-4.69, -10.98) * mm], "startDerivative": vector(-0.18, -0.49) * mm, "endDerivative": vector(-0.65, 0) * mm});
            skFitSpline(sketch, "E200", {"points": [v(-6.5, -7.96) * mm, v(-6.08, -7.84) * mm, v(-5.7, -7.68) * mm, v(-5.11, -7.63) * mm, v(-4.63, -7.74) * mm, v(-4.31, -8.06) * mm, v(-4.21, -8.3) * mm], "startDerivative": vector(2.11, 0.78) * mm, "endDerivative": vector(0.56, -1.73) * mm});
            skFitSpline(sketch, "E201", {"points": [v(-2.04, -8.28) * mm, v(-2.1, -7.91) * mm, v(-2.38, -7.54) * mm, v(-2.92, -7.2) * mm, v(-3.44, -7.03) * mm, v(-4.21, -6.93) * mm, v(-4.64, -6.97) * mm, v(-5.11, -7.07) * mm, v(-5.77, -7.31) * mm, v(-6.08, -7.44) * mm, v(-6.5, -7.64) * mm, v(-6.5, -7.58) * mm, v(-6.5, -7) * mm, v(-6.5, -7) * mm, v(-6.98, -7.03) * mm, v(-8.14, -7.24) * mm, v(-9.31, -7.27) * mm, v(-9.35, -7.27) * mm, v(-9.35, -7.35) * mm, v(-9.36, -7.63) * mm, v(-9.14, -7.61) * mm, v(-8.95, -7.61) * mm, v(-8.67, -7.7) * mm, v(-8.57, -7.94) * mm], "startDerivative": vector(-0.79, 8.64) * mm, "endDerivative": vector(1.7, -7.62) * mm});
            skFitSpline(sketch, "E202", {"points": [v(-6.5, -10.59) * mm, v(-6.34, -10.8) * mm, v(-6.11, -10.98) * mm, v(-5.8, -11) * mm], "startDerivative": vector(0.15, -0.59) * mm, "endDerivative": vector(0.88, 0.06) * mm});
            skFitSpline(sketch, "E203", {"points": [v(-8.57, -10.62) * mm, v(-8.64, -10.84) * mm, v(-8.96, -10.98) * mm, v(-9.34, -11) * mm], "startDerivative": vector(-0.1, -0.84) * mm, "endDerivative": vector(-1.04, 0.02) * mm});
            skFitSpline(sketch, "E204", {"points": [v(-10.44, -9) * mm, v(-10.34, -8.73) * mm, v(-10.36, -8.3) * mm, v(-11.18, -7.32) * mm, v(-12.23, -7.02) * mm, v(-13.54, -6.96) * mm, v(-14.74, -7.23) * mm, v(-15.54, -7.64) * mm, v(-16.34, -8.3) * mm, v(-16.68, -9.2) * mm, v(-16.56, -10.07) * mm, v(-16.02, -10.74) * mm, v(-14.94, -11.26) * mm, v(-13.9, -11.44) * mm, v(-12.63, -11.42) * mm, v(-11.92, -11.25) * mm, v(-11.02, -10.86) * mm, v(-10.57, -10.59) * mm, v(-10.44, -10.43) * mm, v(-10.44, -10.34) * mm, v(-10.67, -10.23) * mm, v(-10.82, -10.22) * mm, v(-11.02, -10.33) * mm, v(-11.3, -10.46) * mm, v(-11.73, -10.59) * mm], "startDerivative": vector(3.96, 9.4) * mm, "endDerivative": vector(-8.98, -1.29) * mm});
            skFitSpline(sketch, "E205", {"points": [v(-11.73, -10.59) * mm, v(-12.1, -10.63) * mm, v(-12.74, -10.65) * mm, v(-13.42, -10.52) * mm, v(-14.08, -10.22) * mm, v(-14.48, -9.7) * mm, v(-14.65, -9.34) * mm, v(-14.7, -9.14) * mm, v(-14.7, -9.01) * mm, v(-14.7, -8.98) * mm, v(-14.61, -9) * mm], "startDerivative": vector(-3.24, -0.47) * mm, "endDerivative": vector(2.24, -0.57) * mm});
            skFitSpline(sketch, "E206", {"points": [v(-14.56, -8.57) * mm, v(-14.56, -8.43) * mm, v(-14.51, -8.16) * mm, v(-14.29, -7.8) * mm, v(-13.96, -7.54) * mm, v(-13.6, -7.4) * mm, v(-12.96, -7.38) * mm, v(-12.75, -7.48) * mm, v(-12.62, -7.6) * mm, v(-12.46, -7.84) * mm, v(-12.34, -8.18) * mm, v(-12.33, -8.4) * mm, v(-12.33, -8.57) * mm, v(-12.39, -8.57) * mm], "startDerivative": vector(-0.08, 2.36) * mm, "endDerivative": vector(-2, 0.56) * mm});
            skLineSegment(sketch, "E207", {"start": v(-30.8, 13.04) * mm, "end": v(1.83, 25.26) * mm});
            skLineSegment(sketch, "E208", {"start": v(1.83, 25.26) * mm, "end": v(34.68, 12.85) * mm});
            skLineSegment(sketch, "E209", {"start": v(-32.25, -12.2) * mm, "end": v(-35.84, -19.3) * mm});
            skLineSegment(sketch, "E210", {"start": v(-34.12, -22.39) * mm, "end": v(29.85, -25.2) * mm});
            skLineSegment(sketch, "E211", {"start": v(31.4, -24.25) * mm, "end": v(40.45, -14.1) * mm});
            skFitSpline(sketch, "E212", {"points": [v(29.85, -25.2) * mm, v(30.3, -25.13) * mm, v(30.78, -24.92) * mm, v(31.4, -24.25) * mm], "startDerivative": vector(1.58, 0.17) * mm, "endDerivative": vector(1.52, 1.9) * mm});
            skFitSpline(sketch, "E213", {"points": [v(40.45, -14.1) * mm, v(40.57, -13.28) * mm, v(40.6, -12.96) * mm, v(40.45, -12.24) * mm, v(39.95, -11.47) * mm, v(38.99, -10.88) * mm, v(38.28, -10.82) * mm, v(37.1, -10.82) * mm, v(36.67, -10.73) * mm, v(35.85, -9.6) * mm, v(35.62, -9.21) * mm, v(35.54, -7.89) * mm, v(35.36, -7.02) * mm, v(34.4, -5.7) * mm, v(33.73, -5.15) * mm, v(33.32, -4.8) * mm, v(33.23, -4.19) * mm, v(33.63, -2.68) * mm, v(33.91, -1.34) * mm, v(33.65, -0.25) * mm, v(33.12, 0.43) * mm, v(32.45, 0.93) * mm, v(31.57, 1.1) * mm, v(31.11, 1.47) * mm, v(30.92, 2.12) * mm, v(31.04, 2.68) * mm, v(32.88, 5.13) * mm, v(33.14, 5.58) * mm, v(33.43, 6.35) * mm, v(33.43, 7.23) * mm, v(33.5, 7.61) * mm, v(33.8, 7.97) * mm, v(34.38, 8.15) * mm, v(34.95, 8.24) * mm, v(35.75, 8.86) * mm, v(36.28, 9.77) * mm, v(36.4, 10.93) * mm, v(35.92, 12.04) * mm, v(35.3, 12.55) * mm, v(34.68, 12.85) * mm], "startDerivative": vector(5.13, 37.38) * mm, "endDerivative": vector(-27.65, 11.7) * mm});
            skFitSpline(sketch, "E214", {"points": [v(-35.84, -19.3) * mm, v(-36, -19.97) * mm, v(-35.72, -21.2) * mm, v(-35.27, -21.84) * mm, v(-34.52, -22.29) * mm, v(-34.12, -22.39) * mm], "startDerivative": vector(-1.26, -3.15) * mm, "endDerivative": vector(2.5, -0.41) * mm});
            skFitSpline(sketch, "E215", {"points": [v(-32.25, -12.2) * mm, v(-31.62, -11.44) * mm, v(-30.95, -11.13) * mm, v(-30, -11.04) * mm, v(-29.54, -10.81) * mm, v(-29.23, -10.06) * mm, v(-29.4, -9.32) * mm, v(-29.42, -8.14) * mm, v(-29.13, -6.62) * mm, v(-28.25, -5.25) * mm, v(-27.57, -4.61) * mm, v(-26.53, -4) * mm, v(-26.07, -3.74) * mm, v(-25.8, -3.39) * mm, v(-25.74, -2.9) * mm, v(-25.77, -2.34) * mm, v(-26.04, -1.83) * mm, v(-26.28, -1.3) * mm, v(-26.57, -0.34) * mm, v(-26.63, 0.38) * mm, v(-26.6, 2.22) * mm, v(-26.6, 2.41) * mm, v(-26.7, 2.63) * mm, v(-27.12, 3.14) * mm, v(-27.43, 3.52) * mm, v(-27.62, 4.7) * mm, v(-27.52, 5.48) * mm, v(-27.08, 6.34) * mm, v(-26.87, 6.67) * mm, v(-26.77, 7.27) * mm, v(-27, 7.9) * mm, v(-27.47, 8.21) * mm, v(-28.14, 8.25) * mm, v(-30.57, 8.28) * mm, v(-30.78, 8.28) * mm, v(-31.29, 8.53) * mm, v(-31.87, 9.12) * mm, v(-32.25, 9.97) * mm, v(-32.35, 10.82) * mm, v(-32.25, 11.41) * mm, v(-31.84, 12.16) * mm, v(-30.8, 13.04) * mm], "startDerivative": vector(22.27, 31.02) * mm, "endDerivative": vector(44.3, 25.13) * mm});
            skSolve(sketch);
        }
        {
            var Q0;
            Q0=makeQuery(id+"F0.imprint","IMPRINT",FACE,{"disambiguationData":[TD([[makeQuery(id+"F0.imprint","IMPRINT",EDGE,{"derivedFrom":sQuery(id+"F0.wireOp",EDGE,"E0")}),1.0]])]});
            var Q1;
            Q1=makeQuery(id+"F0.imprint","IMPRINT",FACE,{"disambiguationData":[TD([[makeQuery(id+"F0.imprint","IMPRINT",EDGE,{"derivedFrom":sQuery(id+"F0.wireOp",EDGE,"E103")}),1.0]])]});
            var Q2;
            Q2=makeQuery(id+"F0.imprint","IMPRINT",FACE,{"disambiguationData":[TD([[makeQuery(id+"F0.imprint","IMPRINT",EDGE,{"derivedFrom":sQuery(id+"F0.wireOp",EDGE,"E58")}),-1.0]])]});
            var Q3;
            Q3=makeQuery(id+"F0.imprint","IMPRINT",FACE,{"disambiguationData":[TD([[makeQuery(id+"F0.imprint","IMPRINT",EDGE,{"derivedFrom":sQuery(id+"F0.wireOp",EDGE,"E0")}),-1.0]])]});
            var Q4;
            Q4=makeQuery(id+"F0.imprint","IMPRINT",FACE,{"disambiguationData":[TD([[makeQuery(id+"F0.imprint","IMPRINT",EDGE,{"derivedFrom":sQuery(id+"F0.wireOp",EDGE,"E3")}),-1.0]])]});
            var Q5;
            Q5=makeQuery(id+"F0.imprint","IMPRINT",FACE,{"disambiguationData":[TD([[makeQuery(id+"F0.imprint","IMPRINT",EDGE,{"derivedFrom":sQuery(id+"F0.wireOp",EDGE,"E7")}),1.0]])]});
            var Q6;
            Q6=makeQuery(id+"F0.imprint","IMPRINT",FACE,{"disambiguationData":[TD([[makeQuery(id+"F0.imprint","IMPRINT",EDGE,{"derivedFrom":sQuery(id+"F0.wireOp",EDGE,"E8")}),1.0]])]});
            var Q7;
            Q7=makeQuery(id+"F0.imprint","IMPRINT",FACE,{"disambiguationData":[TD([[makeQuery(id+"F0.imprint","IMPRINT",EDGE,{"derivedFrom":sQuery(id+"F0.wireOp",EDGE,"E12")}),-1.0]])]});
            var Q8;
            Q8=makeQuery(id+"F0.imprint","IMPRINT",FACE,{"disambiguationData":[TD([[makeQuery(id+"F0.imprint","IMPRINT",EDGE,{"derivedFrom":sQuery(id+"F0.wireOp",EDGE,"E22")}),-1.0]])]});
            var Q9;
            Q9=makeQuery(id+"F0.imprint","IMPRINT",FACE,{"disambiguationData":[TD([[makeQuery(id+"F0.imprint","IMPRINT",EDGE,{"derivedFrom":sQuery(id+"F0.wireOp",EDGE,"E50")}),1.0]])]});
            var Q10;
            Q10=makeQuery(id+"F0.imprint","IMPRINT",FACE,{"disambiguationData":[TD([[makeQuery(id+"F0.imprint","IMPRINT",EDGE,{"derivedFrom":sQuery(id+"F0.wireOp",EDGE,"E69")}),1.0]])]});
            var Q11;
            Q11=makeQuery(id+"F0.imprint","IMPRINT",FACE,{"disambiguationData":[TD([[makeQuery(id+"F0.imprint","IMPRINT",EDGE,{"derivedFrom":sQuery(id+"F0.wireOp",EDGE,"E105")}),1.0]])]});
            var Q12;
            Q12=makeQuery(id+"F0.imprint","IMPRINT",FACE,{"disambiguationData":[TD([[makeQuery(id+"F0.imprint","IMPRINT",EDGE,{"derivedFrom":sQuery(id+"F0.wireOp",EDGE,"E119")}),1.0]])]});
            var Q13;
            Q13=makeQuery(id+"F0.imprint","IMPRINT",FACE,{"disambiguationData":[TD([[makeQuery(id+"F0.imprint","IMPRINT",EDGE,{"derivedFrom":sQuery(id+"F0.wireOp",EDGE,"E131")}),1.0]])]});
            var Q14;
            Q14=makeQuery(id+"F0.imprint","IMPRINT",FACE,{"disambiguationData":[TD([[makeQuery(id+"F0.imprint","IMPRINT",EDGE,{"derivedFrom":sQuery(id+"F0.wireOp",EDGE,"E142")}),1.0]])]});
            var Q15;
            Q15=makeQuery(id+"F0.imprint","IMPRINT",FACE,{"disambiguationData":[TD([[makeQuery(id+"F0.imprint","IMPRINT",EDGE,{"derivedFrom":sQuery(id+"F0.wireOp",EDGE,"E151")}),1.0]])]});
            var Q16;
            Q16=makeQuery(id+"F0.imprint","IMPRINT",FACE,{"disambiguationData":[TD([[makeQuery(id+"F0.imprint","IMPRINT",EDGE,{"derivedFrom":sQuery(id+"F0.wireOp",EDGE,"E103")}),-1.0]])]});
            var Q17;
            Q17=makeQuery(id+"F0.imprint","IMPRINT",FACE,{"disambiguationData":[TD([[makeQuery(id+"F0.imprint","IMPRINT",EDGE,{"derivedFrom":sQuery(id+"F0.wireOp",EDGE,"E102")}),1.0]])]});
            var Q18;
            Q18=makeQuery(id+"F0.imprint","IMPRINT",FACE,{"disambiguationData":[TD([[makeQuery(id+"F0.imprint","IMPRINT",EDGE,{"derivedFrom":sQuery(id+"F0.wireOp",EDGE,"E73")}),1.0]])]});
            extrude(context, id + "F1", {"entities" : qUnion([Q0, Q1, Q2, Q3, Q4, Q5, Q6, Q7, Q8, Q9, Q10, Q11, Q12, Q13, Q14, Q15, Q16, Q17, Q18]), "depth" : 2 * mm, "offsetDistance" : 25 * mm});
        }
        {
            var Q0;
            Q0=makeQuery(id+"F1.opExtrude","CAP_FACE",FACE,{"disambiguationData":[OSD([sQuery(id+"F0.wireOp",EDGE,"E207"),sQuery(id+"F0.wireOp",EDGE,"E208"),sQuery(id+"F0.wireOp",EDGE,"E209"),sQuery(id+"F0.wireOp",EDGE,"E210"),sQuery(id+"F0.wireOp",EDGE,"E211"),sQuery(id+"F0.wireOp",EDGE,"E212"),sQuery(id+"F0.wireOp",EDGE,"E213"),sQuery(id+"F0.wireOp",EDGE,"E214"),sQuery(id+"F0.wireOp",EDGE,"E215")])],"isStart":false});
            var sketch = newSketch(context, id + "F2", { "sketchPlane" : qUnion([Q0])});
            skLineSegment(sketch, "E216.0.0", {"start": v(-30.08, 10.5) * mm, "end": v(33.46, 10.5) * mm});
            skLineSegment(sketch, "E216.0.1", {"start": v(33.46, 10.5) * mm, "end": v(1.83, 22.46) * mm});
            skLineSegment(sketch, "E216.0.2", {"start": v(1.83, 22.46) * mm, "end": v(-30.08, 10.5) * mm});
            skLineSegment(sketch, "E217.0.0", {"start": v(-30.08, -13.2) * mm, "end": v(-33.48, -19.9) * mm});
            skLineSegment(sketch, "E217.0.1", {"start": v(-33.48, -19.9) * mm, "end": v(29.5, -22.68) * mm});
            skLineSegment(sketch, "E217.0.2", {"start": v(29.5, -22.68) * mm, "end": v(37.96, -13.19) * mm});
            skLineSegment(sketch, "E217.0.3", {"start": v(37.96, -13.19) * mm, "end": v(-30.08, -13.2) * mm});
            skLineSegment(sketch, "E218.0.0", {"start": v(21.5, 7.2) * mm, "end": v(20.84, 7.2) * mm});
            skLineSegment(sketch, "E218.0.1", {"start": v(20.84, 7.2) * mm, "end": v(20.84, 3.95) * mm});
            skLineSegment(sketch, "E218.0.2", {"start": v(20.84, 3.95) * mm, "end": v(21.5, 3.95) * mm});
            skFitSpline(sketch, "E218.0.3", {"points": [v(21.5, 3.95) * mm, v(21.51, 4.1) * mm, v(21.55, 4.41) * mm, v(21.77, 4.95) * mm, v(22.09, 5.42) * mm, v(22.62, 5.9) * mm, v(23.03, 6.01) * mm, v(23.23, 6.07) * mm]});
            skLineSegment(sketch, "E218.0.4", {"start": v(23.23, 6.07) * mm, "end": v(27.17, 6.07) * mm});
            skLineSegment(sketch, "E218.0.5", {"start": v(27.17, 6.07) * mm, "end": v(19.8, -3.96) * mm});
            skLineSegment(sketch, "E218.0.6", {"start": v(19.8, -3.96) * mm, "end": v(20, -4.32) * mm});
            skLineSegment(sketch, "E218.0.7", {"start": v(20, -4.32) * mm, "end": v(30.47, -4.32) * mm});
            skLineSegment(sketch, "E218.0.8", {"start": v(30.47, -4.32) * mm, "end": v(31.28, -1.27) * mm});
            skLineSegment(sketch, "E218.0.9", {"start": v(31.28, -1.27) * mm, "end": v(30.49, -1.27) * mm});
            skLineSegment(sketch, "E218.0.10", {"start": v(30.49, -1.27) * mm, "end": v(29.93, -2.28) * mm});
            skFitSpline(sketch, "E218.0.11", {"points": [v(29.93, -2.28) * mm, v(29.87, -2.38) * mm, v(29.71, -2.6) * mm, v(29.29, -3.07) * mm, v(28.87, -3.36) * mm, v(28.28, -3.52) * mm, v(28, -3.5) * mm, v(27.89, -3.5) * mm]});
            skLineSegment(sketch, "E218.0.12", {"start": v(27.89, -3.5) * mm, "end": v(23.51, -3.5) * mm});
            skLineSegment(sketch, "E218.0.13", {"start": v(23.51, -3.5) * mm, "end": v(30.8, 6.4) * mm});
            skLineSegment(sketch, "E218.0.14", {"start": v(30.8, 6.4) * mm, "end": v(30.6, 6.77) * mm});
            skLineSegment(sketch, "E218.0.15", {"start": v(30.6, 6.77) * mm, "end": v(22.29, 6.77) * mm});
            skFitSpline(sketch, "E218.0.16", {"points": [v(22.29, 6.77) * mm, v(22.16, 6.76) * mm, v(21.92, 6.75) * mm, v(21.67, 6.98) * mm, v(21.55, 7.12) * mm, v(21.5, 7.2) * mm]});
            skLineSegment(sketch, "E219.0.0", {"start": v(19.3, -4.23) * mm, "end": v(19.3, -3.75) * mm});
            skLineSegment(sketch, "E219.0.1", {"start": v(19.3, -3.75) * mm, "end": v(18.88, -3.75) * mm});
            skFitSpline(sketch, "E219.0.2", {"points": [v(18.88, -3.75) * mm, v(18.8, -3.73) * mm, v(18.6, -3.7) * mm, v(18.21, -3.52) * mm, v(17.93, -3.36) * mm, v(17.63, -2.99) * mm, v(17.5, -2.8) * mm, v(17.45, -2.7) * mm]});
            skLineSegment(sketch, "E219.0.3", {"start": v(17.45, -2.7) * mm, "end": v(13.26, 6.83) * mm});
            skLineSegment(sketch, "E219.0.4", {"start": v(13.26, 6.83) * mm, "end": v(12.18, 6.83) * mm});
            skLineSegment(sketch, "E219.0.5", {"start": v(12.18, 6.83) * mm, "end": v(7.73, -2.6) * mm});
            skFitSpline(sketch, "E219.0.6", {"points": [v(7.73, -2.6) * mm, v(7.57, -2.9) * mm, v(7.28, -3.48) * mm, v(6.65, -3.8) * mm, v(6.28, -3.77) * mm, v(6.1, -3.75) * mm]});
            skLineSegment(sketch, "E219.0.7", {"start": v(6.1, -3.75) * mm, "end": v(5.78, -3.75) * mm});
            skLineSegment(sketch, "E219.0.8", {"start": v(5.78, -3.75) * mm, "end": v(5.78, -4.23) * mm});
            skLineSegment(sketch, "E219.0.9", {"start": v(5.78, -4.23) * mm, "end": v(10.42, -4.23) * mm});
            skLineSegment(sketch, "E219.0.10", {"start": v(10.42, -4.23) * mm, "end": v(10.42, -3.75) * mm});
            skLineSegment(sketch, "E219.0.11", {"start": v(10.42, -3.75) * mm, "end": v(10.07, -3.75) * mm});
            skFitSpline(sketch, "E219.0.12", {"points": [v(10.07, -3.75) * mm, v(9.82, -3.75) * mm, v(9.53, -3.64) * mm, v(9.11, -3.5) * mm, v(8.97, -3.17) * mm, v(8.97, -3.08) * mm, v(8.99, -3) * mm]});
            skLineSegment(sketch, "E219.0.13", {"start": v(8.99, -3) * mm, "end": v(9.81, -0.88) * mm});
            skLineSegment(sketch, "E219.0.14", {"start": v(9.81, -0.88) * mm, "end": v(13.66, -0.88) * mm});
            skLineSegment(sketch, "E219.0.15", {"start": v(13.66, -0.88) * mm, "end": v(14.56, -3.07) * mm});
            skFitSpline(sketch, "E219.0.16", {"points": [v(14.56, -3.07) * mm, v(14.55, -3.2) * mm, v(14.54, -3.42) * mm, v(14.38, -3.6) * mm, v(14.03, -3.79) * mm, v(13.87, -3.76) * mm, v(13.8, -3.75) * mm]});
            skLineSegment(sketch, "E219.0.17", {"start": v(13.8, -3.75) * mm, "end": v(13.43, -3.75) * mm});
            skLineSegment(sketch, "E219.0.18", {"start": v(13.43, -3.75) * mm, "end": v(13.43, -4.23) * mm});
            skLineSegment(sketch, "E219.0.19", {"start": v(13.43, -4.23) * mm, "end": v(19.3, -4.23) * mm});
            skFitSpline(sketch, "E220.0.2", {"points": [v(18.88, -3.75) * mm, v(18.8, -3.73) * mm, v(18.6, -3.7) * mm, v(18.21, -3.52) * mm, v(17.93, -3.36) * mm, v(17.63, -2.99) * mm, v(17.5, -2.8) * mm, v(17.45, -2.7) * mm]});
            skFitSpline(sketch, "E220.0.6", {"points": [v(7.73, -2.6) * mm, v(7.57, -2.9) * mm, v(7.28, -3.48) * mm, v(6.65, -3.8) * mm, v(6.28, -3.77) * mm, v(6.1, -3.75) * mm]});
            skFitSpline(sketch, "E220.0.12", {"points": [v(10.07, -3.75) * mm, v(9.82, -3.75) * mm, v(9.53, -3.64) * mm, v(9.11, -3.5) * mm, v(8.97, -3.17) * mm, v(8.97, -3.08) * mm, v(8.99, -3) * mm]});
            skFitSpline(sketch, "E220.0.16", {"points": [v(14.56, -3.07) * mm, v(14.55, -3.2) * mm, v(14.54, -3.42) * mm, v(14.38, -3.6) * mm, v(14.03, -3.79) * mm, v(13.87, -3.76) * mm, v(13.8, -3.75) * mm]});
            skLineSegment(sketch, "E221.0.0", {"start": v(10.22, 0) * mm, "end": v(13.22, 0) * mm});
            skLineSegment(sketch, "E221.0.1", {"start": v(13.22, 0) * mm, "end": v(11.72, 3.76) * mm});
            skLineSegment(sketch, "E221.0.2", {"start": v(11.72, 3.76) * mm, "end": v(10.22, 0) * mm});
            skLineSegment(sketch, "E222.0.0", {"start": v(5.21, -4.23) * mm, "end": v(5.21, -3.75) * mm});
            skLineSegment(sketch, "E222.0.1", {"start": v(5.21, -3.75) * mm, "end": v(4.72, -3.75) * mm});
            skFitSpline(sketch, "E222.0.2", {"points": [v(4.72, -3.75) * mm, v(4.62, -3.73) * mm, v(4.4, -3.68) * mm, v(4.04, -3.49) * mm, v(3.68, -3.2) * mm, v(3.57, -2.87) * mm, v(3.5, -2.7) * mm]});
            skLineSegment(sketch, "E222.0.3", {"start": v(3.5, -2.7) * mm, "end": v(3.5, 5.2) * mm});
            skFitSpline(sketch, "E222.0.4", {"points": [v(3.5, 5.2) * mm, v(3.5, 5.32) * mm, v(3.47, 5.56) * mm, v(3.7, 5.88) * mm, v(4.05, 6.18) * mm, v(4.37, 6.19) * mm, v(4.53, 6.19) * mm]});
            skLineSegment(sketch, "E222.0.5", {"start": v(4.53, 6.19) * mm, "end": v(5.27, 6.19) * mm});
            skLineSegment(sketch, "E222.0.6", {"start": v(5.27, 6.19) * mm, "end": v(5.27, 6.7) * mm});
            skLineSegment(sketch, "E222.0.7", {"start": v(5.27, 6.7) * mm, "end": v(-0.88, 6.7) * mm});
            skLineSegment(sketch, "E222.0.8", {"start": v(-0.88, 6.7) * mm, "end": v(-0.88, 6.13) * mm});
            skLineSegment(sketch, "E222.0.9", {"start": v(-0.88, 6.13) * mm, "end": v(-0.41, 6.13) * mm});
            skFitSpline(sketch, "E222.0.10", {"points": [v(-0.41, 6.13) * mm, v(-0.27, 6.14) * mm, v(0, 6.17) * mm, v(0.32, 5.98) * mm, v(0.56, 5.8) * mm, v(0.67, 5.45) * mm, v(0.7, 5.33) * mm, v(0.72, 5.28) * mm]});
            skLineSegment(sketch, "E222.0.11", {"start": v(0.72, 5.28) * mm, "end": v(0.72, 2.06) * mm});
            skLineSegment(sketch, "E222.0.12", {"start": v(0.72, 2.06) * mm, "end": v(-4.27, 2.06) * mm});
            skLineSegment(sketch, "E222.0.13", {"start": v(-4.27, 2.06) * mm, "end": v(-4.27, 5.39) * mm});
            skFitSpline(sketch, "E222.0.14", {"points": [v(-4.27, 5.39) * mm, v(-4.23, 5.55) * mm, v(-4.16, 5.87) * mm, v(-3.74, 6.06) * mm, v(-3.49, 6.13) * mm, v(-3.36, 6.17) * mm]});
            skLineSegment(sketch, "E222.0.15", {"start": v(-3.36, 6.17) * mm, "end": v(-2.66, 6.17) * mm});
            skLineSegment(sketch, "E222.0.16", {"start": v(-2.66, 6.17) * mm, "end": v(-2.66, 6.78) * mm});
            skLineSegment(sketch, "E222.0.17", {"start": v(-2.66, 6.78) * mm, "end": v(-8.85, 6.78) * mm});
            skLineSegment(sketch, "E222.0.18", {"start": v(-8.85, 6.78) * mm, "end": v(-8.85, 6.17) * mm});
            skLineSegment(sketch, "E222.0.19", {"start": v(-8.85, 6.17) * mm, "end": v(-8.39, 6.17) * mm});
            skFitSpline(sketch, "E222.0.20", {"points": [v(-8.39, 6.17) * mm, v(-8.22, 6.19) * mm, v(-7.88, 6.23) * mm, v(-7.32, 5.9) * mm, v(-7.2, 5.54) * mm, v(-7.13, 5.37) * mm]});
            skLineSegment(sketch, "E222.0.21", {"start": v(-7.13, 5.37) * mm, "end": v(-7.13, -2.82) * mm});
            skFitSpline(sketch, "E222.0.22", {"points": [v(-7.13, -2.82) * mm, v(-7.16, -3) * mm, v(-7.23, -3.33) * mm, v(-7.67, -3.64) * mm, v(-8.23, -3.67) * mm, v(-8.42, -3.67) * mm, v(-8.5, -3.66) * mm]});
            skLineSegment(sketch, "E222.0.23", {"start": v(-8.5, -3.66) * mm, "end": v(-8.85, -3.66) * mm});
            skLineSegment(sketch, "E222.0.24", {"start": v(-8.85, -3.66) * mm, "end": v(-8.85, -4.23) * mm});
            skLineSegment(sketch, "E222.0.25", {"start": v(-8.85, -4.23) * mm, "end": v(-2.68, -4.23) * mm});
            skLineSegment(sketch, "E222.0.26", {"start": v(-2.68, -4.23) * mm, "end": v(-2.68, -3.75) * mm});
            skLineSegment(sketch, "E222.0.27", {"start": v(-2.68, -3.75) * mm, "end": v(-3.08, -3.75) * mm});
            skFitSpline(sketch, "E222.0.28", {"points": [v(-3.08, -3.75) * mm, v(-3.33, -3.68) * mm, v(-3.77, -3.54) * mm, v(-4.14, -3.2) * mm, v(-4.24, -2.92) * mm, v(-4.28, -2.78) * mm]});
            skLineSegment(sketch, "E222.0.29", {"start": v(-4.28, -2.78) * mm, "end": v(-4.28, 1.1) * mm});
            skLineSegment(sketch, "E222.0.30", {"start": v(-4.28, 1.1) * mm, "end": v(0.7, 1.1) * mm});
            skLineSegment(sketch, "E222.0.31", {"start": v(0.7, 1.1) * mm, "end": v(0.7, -2.6) * mm});
            skFitSpline(sketch, "E222.0.32", {"points": [v(0.7, -2.6) * mm, v(0.71, -2.8) * mm, v(0.72, -3.2) * mm, v(0.34, -3.75) * mm, v(-0.24, -3.75) * mm, v(-0.53, -3.75) * mm, v(-0.67, -3.75) * mm]});
            skLineSegment(sketch, "E222.0.33", {"start": v(-0.67, -3.75) * mm, "end": v(-1, -3.75) * mm});
            skLineSegment(sketch, "E222.0.34", {"start": v(-1, -3.75) * mm, "end": v(-1, -4.23) * mm});
            skLineSegment(sketch, "E222.0.35", {"start": v(-1, -4.23) * mm, "end": v(5.21, -4.23) * mm});
            skLineSegment(sketch, "E223.0.0", {"start": v(16.2, 8.38) * mm, "end": v(15.06, 9.86) * mm});
            skLineSegment(sketch, "E223.0.1", {"start": v(15.06, 9.86) * mm, "end": v(11.34, 7.83) * mm});
            skLineSegment(sketch, "E223.0.2", {"start": v(11.34, 7.83) * mm, "end": v(11.73, 7.26) * mm});
            skLineSegment(sketch, "E223.0.3", {"start": v(11.73, 7.26) * mm, "end": v(16.2, 8.38) * mm});
            skLineSegment(sketch, "E224.0.0", {"start": v(-14.68, 4.01) * mm, "end": v(-14.68, -2.04) * mm});
            skFitSpline(sketch, "E224.0.1", {"points": [v(-14.68, -2.04) * mm, v(-14.7, -2.3) * mm, v(-14.7, -2.66) * mm, v(-14.64, -2.8) * mm, v(-15.16, -3.35) * mm, v(-15.73, -3.62) * mm, v(-15.94, -3.56) * mm, v(-15.86, -3.66) * mm, v(-15.96, -3.98) * mm, v(-15.75, -3.93) * mm, v(-15.4, -3.97) * mm, v(-14.9, -3.8) * mm, v(-13.68, -3.14) * mm, v(-13.2, -2.5) * mm, v(-12.96, -2) * mm, v(-12.84, -1.76) * mm]});
            skLineSegment(sketch, "E224.0.2", {"start": v(-12.84, -1.76) * mm, "end": v(-12.84, 4) * mm});
            skFitSpline(sketch, "E224.0.3", {"points": [v(-12.84, 4) * mm, v(-12.8, 4.12) * mm, v(-12.73, 4.38) * mm, v(-12.47, 4.39) * mm, v(-12.34, 4.4) * mm]});
            skLineSegment(sketch, "E224.0.4", {"start": v(-12.34, 4.4) * mm, "end": v(-11.81, 4.4) * mm});
            skLineSegment(sketch, "E224.0.5", {"start": v(-11.81, 4.4) * mm, "end": v(-11.81, 4.86) * mm});
            skLineSegment(sketch, "E224.0.6", {"start": v(-11.81, 4.86) * mm, "end": v(-15.63, 4.86) * mm});
            skLineSegment(sketch, "E224.0.7", {"start": v(-15.63, 4.86) * mm, "end": v(-15.63, 4.36) * mm});
            skLineSegment(sketch, "E224.0.8", {"start": v(-15.63, 4.36) * mm, "end": v(-15.1, 4.36) * mm});
            skFitSpline(sketch, "E224.0.9", {"points": [v(-15.1, 4.36) * mm, v(-14.97, 4.4) * mm, v(-14.71, 4.43) * mm, v(-14.7, 4.18) * mm, v(-14.68, 4.01) * mm]});
            skLineSegment(sketch, "E225.0.0", {"start": v(-18.55, 5.87) * mm, "end": v(-19.2, 6.79) * mm});
            skLineSegment(sketch, "E225.0.1", {"start": v(-19.2, 6.79) * mm, "end": v(-21.44, 5.5) * mm});
            skLineSegment(sketch, "E225.0.2", {"start": v(-21.44, 5.5) * mm, "end": v(-21.2, 5.16) * mm});
            skLineSegment(sketch, "E225.0.3", {"start": v(-21.2, 5.16) * mm, "end": v(-18.55, 5.87) * mm});
            skFitSpline(sketch, "E226.0.0", {"points": [v(-25.1, 4.44) * mm, v(-25, 4.37) * mm, v(-24.48, 4.56) * mm, v(-24.19, 4.26) * mm, v(-24.1, 3.92) * mm, v(-24.03, -0.08) * mm, v(-24.08, -0.34) * mm, v(-23.6, -1.8) * mm, v(-21.33, -2.46) * mm, v(-19.3, -2.45) * mm, v(-17.63, -0.88) * mm, v(-17.5, 0.29) * mm, v(-17.4, 3.43) * mm, v(-17.47, 3.9) * mm, v(-17.33, 4.26) * mm, v(-16.72, 4.46) * mm, v(-16.3, 4.28) * mm, v(-16.36, 4.87) * mm, v(-16.52, 4.84) * mm, v(-19.33, 4.89) * mm, v(-19.51, 4.89) * mm, v(-19.5, 4.8) * mm, v(-19.5, 4.48) * mm, v(-19.51, 4.34) * mm, v(-19.2, 4.47) * mm, v(-18.68, 4.43) * mm, v(-18.28, 4.3) * mm, v(-18.17, 3.73) * mm, v(-18.2, 3.58) * mm, v(-18.23, 0.08) * mm, v(-18.17, -0.11) * mm, v(-18.4, -0.7) * mm, v(-19.36, -1.62) * mm, v(-20.85, -1.74) * mm, v(-21.73, -1.2) * mm, v(-22.39, -0.29) * mm, v(-22.28, 0.5) * mm, v(-22.3, 0.62) * mm, v(-22.31, 3.95) * mm, v(-22.25, 4.05) * mm, v(-22.16, 4.4) * mm, v(-21.65, 4.46) * mm, v(-21.35, 4.36) * mm, v(-21.29, 4.61) * mm, v(-21.36, 4.73) * mm, v(-21.32, 4.93) * mm, v(-21.55, 4.83) * mm, v(-24.91, 4.76) * mm, v(-25.1, 4.9) * mm, v(-25.14, 4.71) * mm, v(-25.17, 4.49) * mm, v(-25.1, 4.44) * mm]});
            skFitSpline(sketch, "E227.0.0", {"points": [v(-18.55, -5.16) * mm, v(-18.79, -5.18) * mm, v(-19.52, -5.1) * mm, v(-21.1, -5.06) * mm, v(-21.97, -5.06) * mm, v(-22.58, -5.11) * mm, v(-23.17, -5.22) * mm, v(-23.95, -5.37) * mm, v(-24.9, -5.7) * mm, v(-25.93, -6.21) * mm, v(-26.53, -6.88) * mm, v(-26.9, -7.56) * mm, v(-27.07, -8.38) * mm, v(-26.87, -9.24) * mm, v(-26.6, -9.82) * mm, v(-26, -10.3) * mm, v(-25.25, -10.8) * mm, v(-23.91, -11.28) * mm, v(-22.47, -11.5) * mm, v(-20.87, -11.51) * mm, v(-19.96, -11.42) * mm, v(-19.08, -11.38) * mm, v(-18.61, -11.25) * mm, v(-18.56, -11.28) * mm, v(-18.47, -11.01) * mm, v(-18.1, -10.47) * mm, v(-17.79, -9.8) * mm, v(-17.7, -9.74) * mm, v(-17.82, -9.7) * mm, v(-18.36, -9.7) * mm, v(-18.4, -9.66) * mm, v(-18.47, -9.75) * mm, v(-18.57, -9.9) * mm, v(-18.93, -10.31) * mm, v(-19.68, -10.8) * mm, v(-20.35, -10.98) * mm, v(-21.58, -11.03) * mm, v(-23.04, -10.84) * mm, v(-23.8, -10.05) * mm, v(-24.39, -9.2) * mm, v(-24.57, -7.93) * mm, v(-24.22, -6.97) * mm, v(-23.9, -6.42) * mm, v(-23.04, -5.9) * mm, v(-22.32, -5.61) * mm, v(-21.28, -5.43) * mm, v(-20.47, -5.47) * mm, v(-20, -5.59) * mm, v(-19.33, -5.93) * mm, v(-19, -6.34) * mm, v(-18.67, -6.6) * mm, v(-18.63, -6.8) * mm, v(-18.62, -6.85) * mm, v(-18.53, -6.9) * mm, v(-18.08, -6.85) * mm, v(-18.03, -6.83) * mm, v(-18.1, -6.48) * mm, v(-18.1, -6.12) * mm, v(-18.13, -5.63) * mm, v(-18.15, -5.08) * mm, v(-18.4, -5.15) * mm, v(-18.55, -5.16) * mm]});
            skFitSpline(sketch, "E228.0.0", {"points": [v(-10.44, -9) * mm, v(-10.4, -8.91) * mm, v(-10.32, -8.72) * mm, v(-10.27, -8.24) * mm, v(-11.14, -7.15) * mm, v(-12.22, -7) * mm, v(-13.53, -6.9) * mm, v(-14.76, -7.18) * mm, v(-15.54, -7.62) * mm, v(-16.42, -8.23) * mm, v(-16.75, -9.19) * mm, v(-16.64, -10.1) * mm, v(-16.06, -10.8) * mm, v(-14.93, -11.31) * mm, v(-13.93, -11.47) * mm, v(-12.61, -11.46) * mm, v(-11.94, -11.27) * mm, v(-11.03, -10.88) * mm, v(-10.58, -10.62) * mm, v(-10.44, -10.44) * mm, v(-10.41, -10.32) * mm, v(-10.68, -10.23) * mm, v(-10.82, -10.2) * mm, v(-11.04, -10.34) * mm, v(-11.28, -10.46) * mm, v(-11.62, -10.57) * mm, v(-11.73, -10.59) * mm]});
            skFitSpline(sketch, "E228.0.1", {"points": [v(-11.73, -10.59) * mm, v(-11.84, -10.6) * mm, v(-12.1, -10.64) * mm, v(-12.76, -10.68) * mm, v(-13.42, -10.53) * mm, v(-14.13, -10.3) * mm, v(-14.48, -9.72) * mm, v(-14.66, -9.36) * mm, v(-14.7, -9.15) * mm, v(-14.7, -9.02) * mm, v(-14.7, -8.97) * mm, v(-14.65, -8.99) * mm, v(-14.61, -9) * mm]});
            skLineSegment(sketch, "E228.0.2", {"start": v(-14.61, -9) * mm, "end": v(-10.44, -9) * mm});
            skLineSegment(sketch, "E229.0.0", {"start": v(-1.1, -11.37) * mm, "end": v(-1.1, -10.98) * mm});
            skLineSegment(sketch, "E229.0.1", {"start": v(-1.1, -10.98) * mm, "end": v(-1.33, -10.98) * mm});
            skFitSpline(sketch, "E229.0.2", {"points": [v(-1.33, -10.98) * mm, v(-1.45, -11) * mm, v(-1.67, -11.02) * mm, v(-1.96, -10.85) * mm, v(-2.01, -10.74) * mm, v(-2.04, -10.69) * mm]});
            skLineSegment(sketch, "E229.0.3", {"start": v(-2.04, -10.69) * mm, "end": v(-2.04, -8.28) * mm});
            skFitSpline(sketch, "E229.0.4", {"points": [v(-2.04, -8.28) * mm, v(-2.05, -8.2) * mm, v(-2.06, -8.02) * mm, v(-2.17, -7.76) * mm, v(-2.38, -7.53) * mm, v(-2.68, -7.33) * mm, v(-2.99, -7.17) * mm, v(-3.22, -7.08) * mm, v(-3.44, -7.02) * mm, v(-3.7, -6.97) * mm, v(-3.97, -6.94) * mm, v(-4.22, -6.93) * mm, v(-4.42, -6.94) * mm, v(-4.64, -6.97) * mm, v(-4.87, -7) * mm, v(-5.08, -7.06) * mm, v(-5.26, -7.11) * mm, v(-5.44, -7.18) * mm, v(-5.62, -7.25) * mm, v(-5.78, -7.31) * mm, v(-5.89, -7.36) * mm, v(-5.99, -7.4) * mm, v(-6.12, -7.46) * mm, v(-6.3, -7.55) * mm, v(-6.43, -7.6) * mm, v(-6.5, -7.64) * mm, v(-6.52, -7.64) * mm, v(-6.5, -7.6) * mm, v(-6.5, -7.4) * mm, v(-6.5, -7.2) * mm, v(-6.5, -7.07) * mm, v(-6.5, -7.02) * mm, v(-6.5, -7) * mm, v(-6.5, -7) * mm, v(-6.52, -7) * mm, v(-6.58, -7) * mm, v(-6.68, -7) * mm, v(-6.85, -7.02) * mm, v(-7.07, -7.04) * mm, v(-7.36, -7.1) * mm, v(-7.65, -7.17) * mm, v(-7.98, -7.23) * mm, v(-8.26, -7.26) * mm, v(-8.56, -7.28) * mm, v(-8.85, -7.28) * mm, v(-9.1, -7.28) * mm, v(-9.25, -7.28) * mm, v(-9.32, -7.27) * mm, v(-9.34, -7.27) * mm, v(-9.35, -7.27) * mm, v(-9.35, -7.3) * mm, v(-9.35, -7.33) * mm, v(-9.36, -7.4) * mm, v(-9.38, -7.53) * mm, v(-9.37, -7.64) * mm, v(-9.28, -7.65) * mm, v(-9.16, -7.61) * mm, v(-9.06, -7.6) * mm, v(-8.97, -7.6) * mm, v(-8.86, -7.63) * mm, v(-8.73, -7.66) * mm, v(-8.64, -7.72) * mm, v(-8.6, -7.82) * mm, v(-8.58, -7.9) * mm, v(-8.57, -7.94) * mm]});
            skLineSegment(sketch, "E229.0.5", {"start": v(-8.57, -7.94) * mm, "end": v(-8.57, -10.62) * mm});
            skFitSpline(sketch, "E229.0.6", {"points": [v(-8.57, -10.62) * mm, v(-8.58, -10.7) * mm, v(-8.6, -10.88) * mm, v(-8.97, -11) * mm, v(-9.22, -11) * mm, v(-9.34, -11) * mm]});
            skLineSegment(sketch, "E229.0.7", {"start": v(-9.34, -11) * mm, "end": v(-9.63, -11) * mm});
            skLineSegment(sketch, "E229.0.8", {"start": v(-9.63, -11) * mm, "end": v(-9.63, -11.37) * mm});
            skLineSegment(sketch, "E229.0.9", {"start": v(-9.63, -11.37) * mm, "end": v(-5.63, -11.37) * mm});
            skLineSegment(sketch, "E229.0.10", {"start": v(-5.63, -11.37) * mm, "end": v(-5.63, -10.98) * mm});
            skLineSegment(sketch, "E229.0.11", {"start": v(-5.63, -10.98) * mm, "end": v(-5.8, -11) * mm});
            skFitSpline(sketch, "E229.0.12", {"points": [v(-5.8, -11) * mm, v(-5.9, -11.01) * mm, v(-6.14, -11.02) * mm, v(-6.32, -10.8) * mm, v(-6.5, -10.65) * mm, v(-6.5, -10.59) * mm]});
            skLineSegment(sketch, "E229.0.13", {"start": v(-6.5, -10.59) * mm, "end": v(-6.5, -7.96) * mm});
            skFitSpline(sketch, "E229.0.14", {"points": [v(-6.5, -7.96) * mm, v(-6.39, -7.92) * mm, v(-6.06, -7.86) * mm, v(-5.7, -7.65) * mm, v(-5.1, -7.61) * mm, v(-4.62, -7.69) * mm, v(-4.3, -8.05) * mm, v(-4.24, -8.22) * mm, v(-4.21, -8.3) * mm]});
            skLineSegment(sketch, "E229.0.15", {"start": v(-4.21, -8.3) * mm, "end": v(-4.21, -10.74) * mm});
            skFitSpline(sketch, "E229.0.16", {"points": [v(-4.21, -10.74) * mm, v(-4.23, -10.78) * mm, v(-4.27, -10.89) * mm, v(-4.45, -10.98) * mm, v(-4.6, -10.98) * mm, v(-4.69, -10.98) * mm]});
            skLineSegment(sketch, "E229.0.17", {"start": v(-4.69, -10.98) * mm, "end": v(-4.98, -10.98) * mm});
            skLineSegment(sketch, "E229.0.18", {"start": v(-4.98, -10.98) * mm, "end": v(-4.98, -11.37) * mm});
            skLineSegment(sketch, "E229.0.19", {"start": v(-4.98, -11.37) * mm, "end": v(-1.1, -11.37) * mm});
            skLineSegment(sketch, "E230.0.0", {"start": v(0.43, -7.53) * mm, "end": v(0.43, -10.53) * mm});
            skFitSpline(sketch, "E230.0.1", {"points": [v(0.43, -10.53) * mm, v(0.46, -10.62) * mm, v(0.53, -10.82) * mm, v(0.84, -11.15) * mm, v(1.32, -11.36) * mm, v(2.09, -11.5) * mm, v(2.79, -11.49) * mm, v(3.72, -11.26) * mm, v(4.3, -11.08) * mm, v(4.54, -11.01) * mm, v(4.49, -10.77) * mm, v(4.36, -10.68) * mm, v(4.13, -10.67) * mm, v(3.9, -10.8) * mm, v(3.47, -10.9) * mm, v(3.03, -10.75) * mm, v(2.68, -10.65) * mm, v(2.65, -10.45) * mm, v(2.64, -10.35) * mm]});
            skLineSegment(sketch, "E230.0.2", {"start": v(2.64, -10.35) * mm, "end": v(2.64, -7.53) * mm});
            skLineSegment(sketch, "E230.0.3", {"start": v(2.64, -7.53) * mm, "end": v(4.31, -7.53) * mm});
            skLineSegment(sketch, "E230.0.4", {"start": v(4.31, -7.53) * mm, "end": v(4.31, -7.02) * mm});
            skLineSegment(sketch, "E230.0.5", {"start": v(4.31, -7.02) * mm, "end": v(2.64, -7.02) * mm});
            skLineSegment(sketch, "E230.0.6", {"start": v(2.64, -7.02) * mm, "end": v(2.64, -5.7) * mm});
            skLineSegment(sketch, "E230.0.7", {"start": v(2.64, -5.7) * mm, "end": v(2.15, -5.7) * mm});
            skLineSegment(sketch, "E230.0.8", {"start": v(2.15, -5.7) * mm, "end": v(0.43, -6.4) * mm});
            skLineSegment(sketch, "E230.0.9", {"start": v(0.43, -6.4) * mm, "end": v(0.43, -7.02) * mm});
            skLineSegment(sketch, "E230.0.10", {"start": v(0.43, -7.02) * mm, "end": v(-0.2, -7.02) * mm});
            skLineSegment(sketch, "E230.0.11", {"start": v(-0.2, -7.02) * mm, "end": v(-0.73, -7.53) * mm});
            skLineSegment(sketch, "E230.0.12", {"start": v(-0.73, -7.53) * mm, "end": v(0.43, -7.53) * mm});
            skLineSegment(sketch, "E231.0.0", {"start": v(19.3, -10.56) * mm, "end": v(19.3, -7.08) * mm});
            skLineSegment(sketch, "E231.0.1", {"start": v(19.3, -7.08) * mm, "end": v(16.1, -7.17) * mm});
            skLineSegment(sketch, "E231.0.2", {"start": v(16.1, -7.17) * mm, "end": v(16.11, -7.5) * mm});
            skFitSpline(sketch, "E231.0.3", {"points": [v(16.11, -7.5) * mm, v(16.17, -7.5) * mm, v(16.3, -7.5) * mm, v(16.55, -7.49) * mm, v(16.85, -7.58) * mm, v(17, -7.7) * mm, v(17.07, -7.77) * mm]});
            skLineSegment(sketch, "E231.0.4", {"start": v(17.07, -7.77) * mm, "end": v(17.07, -10.43) * mm});
            skFitSpline(sketch, "E231.0.5", {"points": [v(17.07, -10.43) * mm, v(16.98, -10.5) * mm, v(16.8, -10.62) * mm, v(16.51, -10.7) * mm, v(16.11, -10.76) * mm, v(15.7, -10.74) * mm, v(15.4, -10.7) * mm, v(15.03, -10.42) * mm, v(14.92, -10.18) * mm, v(14.88, -10) * mm, v(14.85, -9.91) * mm]});
            skLineSegment(sketch, "E231.0.6", {"start": v(14.85, -9.91) * mm, "end": v(14.85, -7.04) * mm});
            skLineSegment(sketch, "E231.0.7", {"start": v(14.85, -7.04) * mm, "end": v(11.89, -7.14) * mm});
            skLineSegment(sketch, "E231.0.8", {"start": v(11.89, -7.14) * mm, "end": v(11.9, -7.54) * mm});
            skFitSpline(sketch, "E231.0.9", {"points": [v(11.9, -7.54) * mm, v(11.97, -7.53) * mm, v(12.1, -7.52) * mm, v(12.4, -7.59) * mm, v(12.66, -7.66) * mm, v(12.73, -7.8) * mm, v(12.77, -7.86) * mm]});
            skLineSegment(sketch, "E231.0.10", {"start": v(12.77, -7.86) * mm, "end": v(12.77, -10.35) * mm});
            skFitSpline(sketch, "E231.0.11", {"points": [v(12.77, -10.35) * mm, v(12.76, -10.4) * mm, v(12.75, -10.5) * mm, v(12.83, -10.67) * mm, v(12.97, -10.9) * mm, v(13.38, -11.16) * mm, v(13.88, -11.42) * mm, v(14.52, -11.48) * mm, v(15.33, -11.52) * mm, v(15.84, -11.37) * mm, v(16.43, -11.17) * mm, v(16.74, -10.98) * mm, v(16.95, -10.91) * mm, v(17.06, -10.88) * mm]});
            skLineSegment(sketch, "E231.0.12", {"start": v(17.06, -10.88) * mm, "end": v(17.06, -11.45) * mm});
            skFitSpline(sketch, "E231.0.13", {"points": [v(17.06, -11.45) * mm, v(17.2, -11.4) * mm, v(17.72, -11.32) * mm, v(18.21, -11.26) * mm, v(18.8, -11.18) * mm, v(19.54, -11.08) * mm, v(20.23, -11.1) * mm, v(20.28, -11.1) * mm, v(20.27, -10.9) * mm, v(20.28, -10.65) * mm, v(19.9, -10.77) * mm, v(19.41, -10.66) * mm, v(19.3, -10.56) * mm]});
            skFitSpline(sketch, "E232.0.0", {"points": [v(30.73, -10.82) * mm, v(30.7, -10.9) * mm, v(30.6, -10.96) * mm, v(30.39, -11.02) * mm, v(30.28, -11.01) * mm, v(30.22, -11) * mm]});
            skLineSegment(sketch, "E232.0.1", {"start": v(30.22, -11) * mm, "end": v(29.94, -11) * mm});
            skLineSegment(sketch, "E232.0.2", {"start": v(29.94, -11) * mm, "end": v(29.94, -11.4) * mm});
            skLineSegment(sketch, "E232.0.3", {"start": v(29.94, -11.4) * mm, "end": v(33.83, -11.4) * mm});
            skLineSegment(sketch, "E232.0.4", {"start": v(33.83, -11.4) * mm, "end": v(33.83, -10.97) * mm});
            skLineSegment(sketch, "E232.0.5", {"start": v(33.83, -10.97) * mm, "end": v(33.61, -10.98) * mm});
            skFitSpline(sketch, "E232.0.6", {"points": [v(33.61, -10.98) * mm, v(33.55, -10.98) * mm, v(33.42, -11) * mm, v(33.08, -10.88) * mm, v(32.99, -10.79) * mm, v(32.95, -10.75) * mm]});
            skLineSegment(sketch, "E232.0.7", {"start": v(32.95, -10.75) * mm, "end": v(32.95, -8.3) * mm});
            skFitSpline(sketch, "E232.0.8", {"points": [v(32.95, -8.3) * mm, v(32.92, -8.16) * mm, v(32.87, -7.9) * mm, v(32.68, -7.57) * mm, v(32.23, -7.23) * mm, v(31.7, -7.1) * mm, v(31.1, -6.95) * mm, v(30.3, -6.96) * mm, v(29.7, -7.14) * mm, v(29.1, -7.38) * mm, v(28.7, -7.6) * mm, v(28.42, -7.77) * mm, v(28.35, -7.8) * mm, v(28.32, -7.67) * mm, v(27.99, -7.28) * mm, v(27.45, -7.02) * mm, v(26.8, -6.93) * mm, v(25.9, -6.97) * mm, v(25.42, -7.1) * mm, v(24.68, -7.37) * mm, v(24.43, -7.52) * mm, v(24.24, -7.59) * mm, v(24.15, -7.62) * mm]});
            skLineSegment(sketch, "E232.0.9", {"start": v(24.15, -7.62) * mm, "end": v(24.15, -6.96) * mm});
            skFitSpline(sketch, "E232.0.10", {"points": [v(24.15, -6.96) * mm, v(24.1, -6.99) * mm, v(23.9, -7.07) * mm, v(22.77, -7.22) * mm, v(22.1, -7.23) * mm, v(21.75, -7.23) * mm]});
            skLineSegment(sketch, "E232.0.11", {"start": v(21.75, -7.23) * mm, "end": v(21.11, -7.23) * mm});
            skLineSegment(sketch, "E232.0.12", {"start": v(21.11, -7.23) * mm, "end": v(21.12, -7.6) * mm});
            skLineSegment(sketch, "E232.0.13", {"start": v(21.12, -7.6) * mm, "end": v(21.56, -7.6) * mm});
            skFitSpline(sketch, "E232.0.14", {"points": [v(21.56, -7.6) * mm, v(21.6, -7.61) * mm, v(21.68, -7.65) * mm, v(21.87, -7.76) * mm, v(21.91, -7.85) * mm, v(21.94, -7.89) * mm]});
            skLineSegment(sketch, "E232.0.15", {"start": v(21.94, -7.89) * mm, "end": v(21.94, -10.72) * mm});
            skFitSpline(sketch, "E232.0.16", {"points": [v(21.94, -10.72) * mm, v(21.92, -10.76) * mm, v(21.87, -10.82) * mm, v(21.69, -10.96) * mm, v(21.26, -11.03) * mm, v(21.13, -11.02) * mm, v(21.07, -11.02) * mm]});
            skLineSegment(sketch, "E232.0.17", {"start": v(21.07, -11.02) * mm, "end": v(20.93, -11.02) * mm});
            skLineSegment(sketch, "E232.0.18", {"start": v(20.93, -11.02) * mm, "end": v(20.93, -11.4) * mm});
            skLineSegment(sketch, "E232.0.19", {"start": v(20.93, -11.4) * mm, "end": v(24.9, -11.4) * mm});
            skLineSegment(sketch, "E232.0.20", {"start": v(24.9, -11.4) * mm, "end": v(24.88, -11) * mm});
            skLineSegment(sketch, "E232.0.21", {"start": v(24.88, -11) * mm, "end": v(24.61, -11.02) * mm});
            skFitSpline(sketch, "E232.0.22", {"points": [v(24.61, -11.02) * mm, v(24.58, -11.02) * mm, v(24.5, -11) * mm, v(24.28, -10.98) * mm, v(24.16, -10.87) * mm, v(24.13, -10.79) * mm, v(24.11, -10.75) * mm]});
            skLineSegment(sketch, "E232.0.23", {"start": v(24.11, -10.75) * mm, "end": v(24.11, -8.08) * mm});
            skFitSpline(sketch, "E232.0.24", {"points": [v(24.11, -8.08) * mm, v(24.13, -8.04) * mm, v(24.18, -7.95) * mm, v(24.37, -7.84) * mm, v(24.91, -7.68) * mm, v(25.25, -7.68) * mm, v(25.88, -7.8) * mm, v(26.05, -7.95) * mm, v(26.25, -8.12) * mm, v(26.29, -8.25) * mm, v(26.3, -8.31) * mm]});
            skLineSegment(sketch, "E232.0.25", {"start": v(26.3, -8.31) * mm, "end": v(26.3, -10.76) * mm});
            skFitSpline(sketch, "E232.0.26", {"points": [v(26.3, -10.76) * mm, v(26.29, -10.8) * mm, v(26.24, -10.87) * mm, v(26.05, -10.96) * mm, v(25.88, -11.02) * mm, v(25.78, -11) * mm, v(25.73, -11) * mm]});
            skLineSegment(sketch, "E232.0.27", {"start": v(25.73, -11) * mm, "end": v(25.55, -11) * mm});
            skLineSegment(sketch, "E232.0.28", {"start": v(25.55, -11) * mm, "end": v(25.55, -11.4) * mm});
            skLineSegment(sketch, "E232.0.29", {"start": v(25.55, -11.4) * mm, "end": v(29.38, -11.4) * mm});
            skLineSegment(sketch, "E232.0.30", {"start": v(29.38, -11.4) * mm, "end": v(29.36, -11) * mm});
            skLineSegment(sketch, "E232.0.31", {"start": v(29.36, -11) * mm, "end": v(29.06, -11.02) * mm});
            skFitSpline(sketch, "E232.0.32", {"points": [v(29.06, -11.02) * mm, v(28.98, -11) * mm, v(28.84, -10.98) * mm, v(28.67, -10.9) * mm, v(28.6, -10.79) * mm, v(28.55, -10.73) * mm]});
            skLineSegment(sketch, "E232.0.33", {"start": v(28.55, -10.73) * mm, "end": v(28.55, -8.04) * mm});
            skFitSpline(sketch, "E232.0.34", {"points": [v(28.55, -8.04) * mm, v(28.6, -8.01) * mm, v(28.7, -7.93) * mm, v(29.25, -7.74) * mm, v(29.58, -7.73) * mm, v(29.96, -7.7) * mm, v(30.44, -7.83) * mm, v(30.72, -8.13) * mm, v(30.7, -8.3) * mm, v(30.73, -8.35) * mm]});
            skLineSegment(sketch, "E232.0.35", {"start": v(30.73, -8.35) * mm, "end": v(30.73, -10.82) * mm});
            skFitSpline(sketch, "E233.0.0", {"points": [v(8.26, -8.42) * mm, v(8.34, -8.38) * mm, v(8.52, -8.27) * mm, v(8.86, -8.07) * mm, v(9.04, -7.98) * mm, v(9.38, -8.01) * mm, v(9.58, -8.11) * mm, v(9.8, -8.28) * mm, v(10.04, -8.39) * mm, v(10.55, -8.3) * mm, v(10.8, -8.18) * mm, v(11.07, -7.95) * mm, v(11.15, -7.65) * mm, v(11.18, -7.45) * mm, v(11.02, -7.23) * mm, v(10.76, -7.05) * mm, v(10.4, -6.93) * mm, v(9.84, -6.93) * mm, v(9.4, -7.03) * mm, v(9.11, -7.22) * mm, v(8.75, -7.43) * mm, v(8.42, -7.77) * mm, v(8.3, -7.88) * mm, v(8.26, -7.93) * mm]});
            skLineSegment(sketch, "E233.0.1", {"start": v(8.26, -7.93) * mm, "end": v(8.26, -6.9) * mm});
            skFitSpline(sketch, "E233.0.2", {"points": [v(8.26, -6.9) * mm, v(8.08, -6.94) * mm, v(7.85, -6.97) * mm, v(7.25, -7.13) * mm, v(6.73, -7.23) * mm, v(6.31, -7.3) * mm, v(6.19, -7.3) * mm, v(6.13, -7.3) * mm]});
            skLineSegment(sketch, "E233.0.3", {"start": v(6.13, -7.3) * mm, "end": v(5.24, -7.3) * mm});
            skLineSegment(sketch, "E233.0.4", {"start": v(5.24, -7.3) * mm, "end": v(5.24, -7.62) * mm});
            skLineSegment(sketch, "E233.0.5", {"start": v(5.24, -7.62) * mm, "end": v(5.53, -7.62) * mm});
            skFitSpline(sketch, "E233.0.6", {"points": [v(5.53, -7.62) * mm, v(5.57, -7.63) * mm, v(5.67, -7.65) * mm, v(5.95, -7.71) * mm, v(6.09, -7.86) * mm, v(6.12, -8) * mm, v(6.13, -8.07) * mm]});
            skLineSegment(sketch, "E233.0.7", {"start": v(6.13, -8.07) * mm, "end": v(6.13, -10.53) * mm});
            skFitSpline(sketch, "E233.0.8", {"points": [v(6.13, -10.53) * mm, v(6.11, -10.58) * mm, v(6.08, -10.68) * mm, v(5.98, -10.84) * mm, v(5.75, -10.98) * mm, v(5.5, -11.02) * mm, v(5.4, -11.01) * mm, v(5.37, -11) * mm]});
            skLineSegment(sketch, "E233.0.9", {"start": v(5.37, -11) * mm, "end": v(5.06, -11) * mm});
            skLineSegment(sketch, "E233.0.10", {"start": v(5.06, -11) * mm, "end": v(5.06, -11.36) * mm});
            skLineSegment(sketch, "E233.0.11", {"start": v(5.06, -11.36) * mm, "end": v(9.5, -11.36) * mm});
            skLineSegment(sketch, "E233.0.12", {"start": v(9.5, -11.36) * mm, "end": v(9.5, -10.98) * mm});
            skLineSegment(sketch, "E233.0.13", {"start": v(9.5, -10.98) * mm, "end": v(8.93, -10.98) * mm});
            skFitSpline(sketch, "E233.0.14", {"points": [v(8.93, -10.98) * mm, v(8.86, -10.98) * mm, v(8.71, -10.97) * mm, v(8.46, -10.9) * mm, v(8.3, -10.8) * mm, v(8.28, -10.67) * mm, v(8.26, -10.6) * mm]});
            skLineSegment(sketch, "E233.0.15", {"start": v(8.26, -10.6) * mm, "end": v(8.26, -8.42) * mm});
            skFitSpline(sketch, "E234.0.0", {"points": [v(-12.39, -8.57) * mm, v(-12.36, -8.58) * mm, v(-12.3, -8.6) * mm, v(-12.34, -8.38) * mm, v(-12.32, -8.18) * mm, v(-12.45, -7.84) * mm, v(-12.6, -7.6) * mm, v(-12.75, -7.47) * mm, v(-12.96, -7.34) * mm, v(-13.63, -7.36) * mm, v(-13.96, -7.52) * mm, v(-14.3, -7.8) * mm, v(-14.53, -8.14) * mm, v(-14.57, -8.42) * mm, v(-14.57, -8.53) * mm, v(-14.56, -8.57) * mm]});
            skLineSegment(sketch, "E234.0.1", {"start": v(-14.56, -8.57) * mm, "end": v(-12.39, -8.57) * mm});
            skSolve(sketch);
        }
        {
            var Q0;
            Q0=makeQuery(id+"F2.imprint","IMPRINT",FACE,{"disambiguationData":[TD([[makeQuery(id+"F2.imprint","IMPRINT",EDGE,{"derivedFrom":sQuery(id+"F2.wireOp",EDGE,"E222.0.0")}),1.0]])]});
            var Q1;
            Q1=makeQuery(id+"F2.imprint","IMPRINT",FACE,{"disambiguationData":[TD([[makeQuery(id+"F2.imprint","IMPRINT",EDGE,{"derivedFrom":sQuery(id+"F2.wireOp",EDGE,"E219.0.0")}),1.0]])]});
            var Q2;
            Q2=makeQuery(id+"F2.imprint","IMPRINT",FACE,{"disambiguationData":[TD([[makeQuery(id+"F2.imprint","IMPRINT",EDGE,{"derivedFrom":sQuery(id+"F2.wireOp",EDGE,"E223.0.0")}),1.0]])]});
            var Q3;
            Q3=makeQuery(id+"F2.imprint","IMPRINT",FACE,{"disambiguationData":[TD([[makeQuery(id+"F2.imprint","IMPRINT",EDGE,{"derivedFrom":sQuery(id+"F2.wireOp",EDGE,"E218.0.0")}),1.0]])]});
            var Q4;
            Q4=makeQuery(id+"F2.imprint","IMPRINT",FACE,{"disambiguationData":[TD([[makeQuery(id+"F2.imprint","IMPRINT",EDGE,{"derivedFrom":sQuery(id+"F2.wireOp",EDGE,"E227.0.0")}),1.0]])]});
            var Q5;
            Q5=makeQuery(id+"F2.imprint","IMPRINT",FACE,{"disambiguationData":[TD([[makeQuery(id+"F2.imprint","IMPRINT",EDGE,{"derivedFrom":sQuery(id+"F2.wireOp",EDGE,"E228.0.0")}),1.0]])]});
            var Q6;
            Q6=makeQuery(id+"F2.imprint","IMPRINT",FACE,{"disambiguationData":[TD([[makeQuery(id+"F2.imprint","IMPRINT",EDGE,{"derivedFrom":sQuery(id+"F2.wireOp",EDGE,"E229.0.0")}),1.0]])]});
            var Q7;
            Q7=makeQuery(id+"F2.imprint","IMPRINT",FACE,{"disambiguationData":[TD([[makeQuery(id+"F2.imprint","IMPRINT",EDGE,{"derivedFrom":sQuery(id+"F2.wireOp",EDGE,"E230.0.0")}),1.0]])]});
            var Q8;
            Q8=makeQuery(id+"F2.imprint","IMPRINT",FACE,{"disambiguationData":[TD([[makeQuery(id+"F2.imprint","IMPRINT",EDGE,{"derivedFrom":sQuery(id+"F2.wireOp",EDGE,"E233.0.0")}),1.0]])]});
            var Q9;
            Q9=makeQuery(id+"F2.imprint","IMPRINT",FACE,{"disambiguationData":[TD([[makeQuery(id+"F2.imprint","IMPRINT",EDGE,{"derivedFrom":sQuery(id+"F2.wireOp",EDGE,"E231.0.0")}),1.0]])]});
            var Q10;
            Q10=makeQuery(id+"F2.imprint","IMPRINT",FACE,{"disambiguationData":[TD([[makeQuery(id+"F2.imprint","IMPRINT",EDGE,{"derivedFrom":sQuery(id+"F2.wireOp",EDGE,"E232.0.0")}),1.0]])]});
            extrude(context, id + "F3", {"entities" : qUnion([Q0, Q1, Q2, Q3, Q4, Q5, Q6, Q7, Q8, Q9, Q10]), "operationType" : NewBodyOperationType.ADD, "depth" : .8 * mm, "offsetDistance" : 25 * mm});
        }
        {
            var Q0;
            Q0=makeQuery(id+"F1.opExtrude","SWEPT_BODY",BODY,{"disambiguationData":[OSD([sQuery(id+"F0.wireOp",EDGE,"E207"),sQuery(id+"F0.wireOp",EDGE,"E208"),sQuery(id+"F0.wireOp",EDGE,"E209"),sQuery(id+"F0.wireOp",EDGE,"E210"),sQuery(id+"F0.wireOp",EDGE,"E211"),sQuery(id+"F0.wireOp",EDGE,"E212"),sQuery(id+"F0.wireOp",EDGE,"E213"),sQuery(id+"F0.wireOp",EDGE,"E214"),sQuery(id+"F0.wireOp",EDGE,"E215")])]});
            var Q1;
            Q1=qCreatedBy(makeId("Origin.pointOp"),VERTEX);
            transform(context, id + "F4", {"entities" : qUnion([Q0]), "transformType" : TransformType.SCALE_UNIFORMLY, "scale" : 1.8, "scalePoint" : qUnion([Q1]), "makeCopy" : true});
        }
    });
